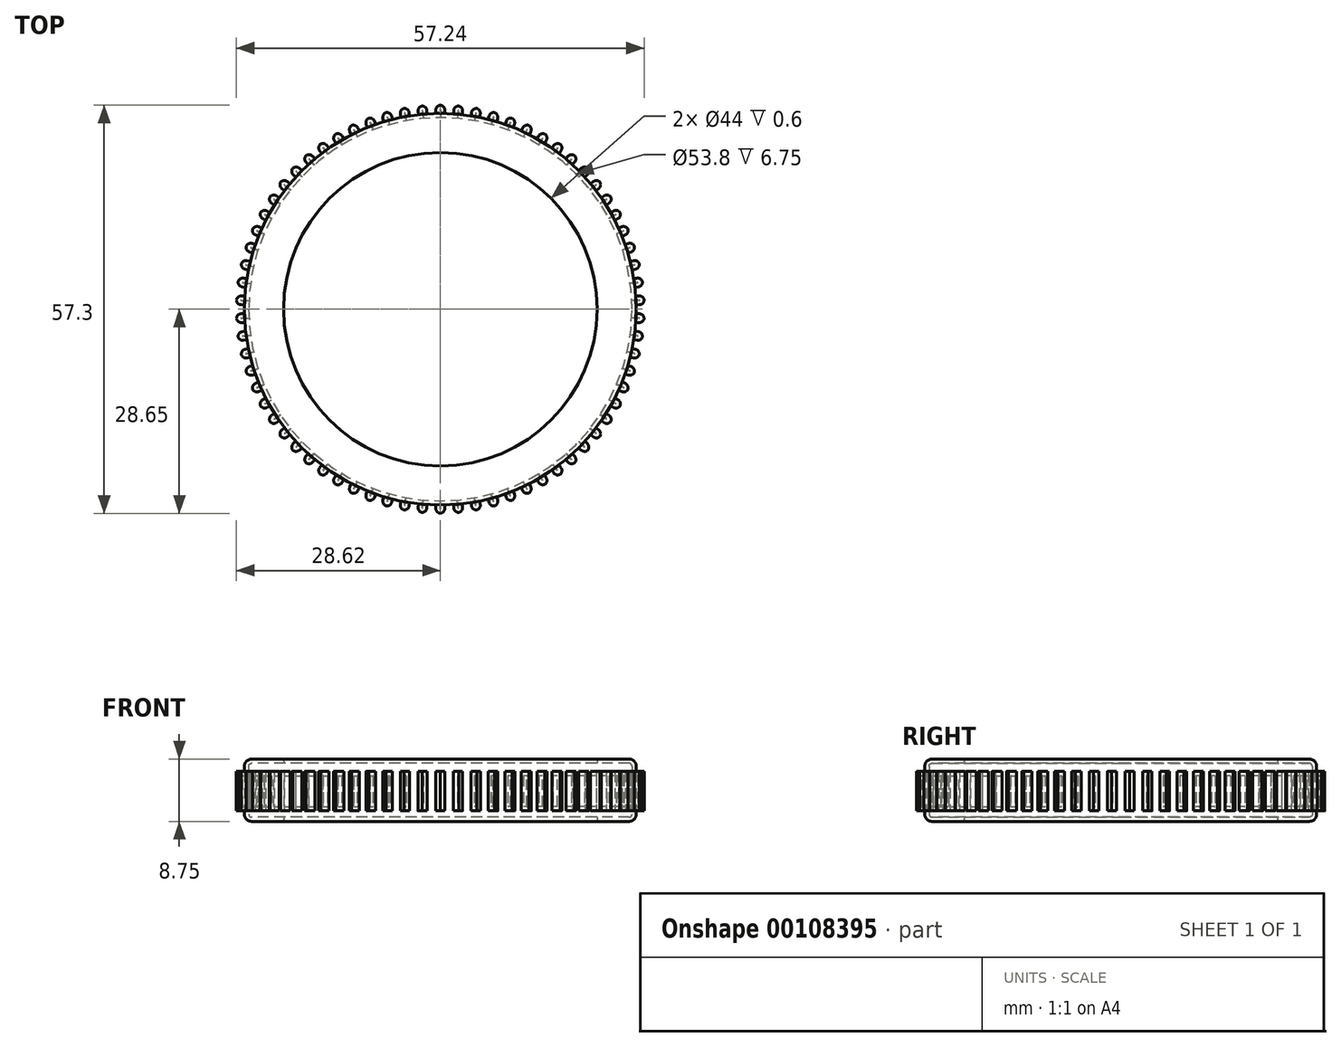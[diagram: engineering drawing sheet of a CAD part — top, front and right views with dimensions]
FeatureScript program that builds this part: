
annotation { "Feature Type Name" : "Feature", "Feature Type Description" : "" }
export const myFeature = defineFeature(function(context is Context, id is Id, definition is map)
    precondition{}
    {
        {
            var Q0;
            Q0=qCreatedBy(makeId("Top.planeOp"),FACE);
            var sketch = newSketch(context, id + "F0", { "sketchPlane" : qUnion([Q0])});
            skCircle(sketch, "E0", {"center": v(0, 0) * mm, "radius": 27.5 * mm});
            skCircle(sketch, "E1", {"center": v(0, 0) * mm, "radius": 22 * mm});
            skLineSegment(sketch, "E2", {"start": v(0, 0) * mm, "end": v(0, 27.5) * mm});
            skLineSegment(sketch, "E3", {"start": v(0, 28.65) * mm, "end": v(0.62, 28.65) * mm});
            skLineSegment(sketch, "E4", {"start": v(0, 28.65) * mm, "end": v(-0.62, 28.65) * mm});
            skLineSegment(sketch, "E5", {"start": v(-0.62, 28.65) * mm, "end": v(-0.62, 27.5) * mm});
            skLineSegment(sketch, "E6", {"start": v(0.62, 28.65) * mm, "end": v(0.62, 27.5) * mm});
            skLineSegment(sketch, "E7.1.0", {"start": v(-3.2, 28.48) * mm, "end": v(-3.09, 27.33) * mm});
            skLineSegment(sketch, "E7.1.1", {"start": v(-2.57, 28.53) * mm, "end": v(-3.2, 28.48) * mm});
            skLineSegment(sketch, "E7.1.2", {"start": v(-2.57, 28.53) * mm, "end": v(-1.95, 28.6) * mm});
            skLineSegment(sketch, "E7.1.3", {"start": v(-1.95, 28.6) * mm, "end": v(-1.84, 27.44) * mm});
            skLineSegment(sketch, "E7.2.0", {"start": v(-5.73, 28.08) * mm, "end": v(-5.52, 26.94) * mm});
            skLineSegment(sketch, "E7.2.1", {"start": v(-5.12, 28.19) * mm, "end": v(-5.73, 28.08) * mm});
            skLineSegment(sketch, "E7.2.2", {"start": v(-5.12, 28.19) * mm, "end": v(-4.5, 28.3) * mm});
            skLineSegment(sketch, "E7.2.3", {"start": v(-4.5, 28.3) * mm, "end": v(-4.3, 27.16) * mm});
            skLineSegment(sketch, "E7.3.0", {"start": v(-8.22, 27.45) * mm, "end": v(-7.92, 26.34) * mm});
            skLineSegment(sketch, "E7.3.1", {"start": v(-7.62, 27.62) * mm, "end": v(-8.22, 27.45) * mm});
            skLineSegment(sketch, "E7.3.2", {"start": v(-7.62, 27.62) * mm, "end": v(-7.02, 27.78) * mm});
            skLineSegment(sketch, "E7.3.3", {"start": v(-7.02, 27.78) * mm, "end": v(-6.71, 26.67) * mm});
            skLineSegment(sketch, "E7.4.0", {"start": v(-10.65, 26.6) * mm, "end": v(-10.25, 25.52) * mm});
            skLineSegment(sketch, "E7.4.1", {"start": v(-10.07, 26.82) * mm, "end": v(-10.65, 26.6) * mm});
            skLineSegment(sketch, "E7.4.2", {"start": v(-10.07, 26.82) * mm, "end": v(-9.48, 27.04) * mm});
            skLineSegment(sketch, "E7.4.3", {"start": v(-9.48, 27.04) * mm, "end": v(-9.08, 25.96) * mm});
            skLineSegment(sketch, "E7.5.0", {"start": v(-13, 25.54) * mm, "end": v(-12.5, 24.5) * mm});
            skLineSegment(sketch, "E7.5.1", {"start": v(-12.43, 25.81) * mm, "end": v(-13, 25.54) * mm});
            skLineSegment(sketch, "E7.5.2", {"start": v(-12.43, 25.81) * mm, "end": v(-11.87, 26.08) * mm});
            skLineSegment(sketch, "E7.5.3", {"start": v(-11.87, 26.08) * mm, "end": v(-11.37, 25.04) * mm});
            skLineSegment(sketch, "E7.6.0", {"start": v(-15.23, 24.27) * mm, "end": v(-14.64, 23.28) * mm});
            skLineSegment(sketch, "E7.6.1", {"start": v(-14.7, 24.6) * mm, "end": v(-15.23, 24.27) * mm});
            skLineSegment(sketch, "E7.6.2", {"start": v(-14.7, 24.6) * mm, "end": v(-14.16, 24.92) * mm});
            skLineSegment(sketch, "E7.6.3", {"start": v(-14.16, 24.92) * mm, "end": v(-13.56, 23.92) * mm});
            skLineSegment(sketch, "E7.7.0", {"start": v(-17.35, 22.81) * mm, "end": v(-16.67, 21.87) * mm});
            skLineSegment(sketch, "E7.7.1", {"start": v(-16.84, 23.18) * mm, "end": v(-17.35, 22.81) * mm});
            skLineSegment(sketch, "E7.7.2", {"start": v(-16.84, 23.18) * mm, "end": v(-16.33, 23.55) * mm});
            skLineSegment(sketch, "E7.7.3", {"start": v(-16.33, 23.55) * mm, "end": v(-15.65, 22.6) * mm});
            skLineSegment(sketch, "E7.8.0", {"start": v(-19.32, 21.16) * mm, "end": v(-18.56, 20.3) * mm});
            skLineSegment(sketch, "E7.8.1", {"start": v(-18.85, 21.58) * mm, "end": v(-19.32, 21.16) * mm});
            skLineSegment(sketch, "E7.8.2", {"start": v(-18.85, 21.58) * mm, "end": v(-18.38, 21.99) * mm});
            skLineSegment(sketch, "E7.8.3", {"start": v(-18.38, 21.99) * mm, "end": v(-17.62, 21.12) * mm});
            skLineSegment(sketch, "E7.9.0", {"start": v(-21.14, 19.35) * mm, "end": v(-20.3, 18.55) * mm});
            skLineSegment(sketch, "E7.9.1", {"start": v(-20.7, 19.8) * mm, "end": v(-21.14, 19.35) * mm});
            skLineSegment(sketch, "E7.9.2", {"start": v(-20.7, 19.8) * mm, "end": v(-20.28, 20.25) * mm});
            skLineSegment(sketch, "E7.9.3", {"start": v(-20.28, 20.25) * mm, "end": v(-19.44, 19.45) * mm});
            skLineSegment(sketch, "E7.10.0", {"start": v(-22.79, 17.37) * mm, "end": v(-21.88, 16.65) * mm});
            skLineSegment(sketch, "E7.10.1", {"start": v(-22.4, 17.86) * mm, "end": v(-22.79, 17.37) * mm});
            skLineSegment(sketch, "E7.10.2", {"start": v(-22.4, 17.86) * mm, "end": v(-22, 18.35) * mm});
            skLineSegment(sketch, "E7.10.3", {"start": v(-22, 18.35) * mm, "end": v(-21.1, 17.63) * mm});
            skLineSegment(sketch, "E7.11.0", {"start": v(-24.25, 15.26) * mm, "end": v(-23.29, 14.62) * mm});
            skLineSegment(sketch, "E7.11.1", {"start": v(-23.91, 15.78) * mm, "end": v(-24.25, 15.26) * mm});
            skLineSegment(sketch, "E7.11.2", {"start": v(-23.91, 15.78) * mm, "end": v(-23.57, 16.3) * mm});
            skLineSegment(sketch, "E7.11.3", {"start": v(-23.57, 16.3) * mm, "end": v(-22.6, 15.67) * mm});
            skLineSegment(sketch, "E7.12.0", {"start": v(-25.53, 13.03) * mm, "end": v(-24.5, 12.48) * mm});
            skLineSegment(sketch, "E7.12.1", {"start": v(-25.23, 13.58) * mm, "end": v(-25.53, 13.03) * mm});
            skLineSegment(sketch, "E7.12.2", {"start": v(-25.23, 13.58) * mm, "end": v(-24.93, 14.13) * mm});
            skLineSegment(sketch, "E7.12.3", {"start": v(-24.93, 14.13) * mm, "end": v(-23.91, 13.58) * mm});
            skLineSegment(sketch, "E7.13.0", {"start": v(-26.6, 10.69) * mm, "end": v(-25.53, 10.23) * mm});
            skLineSegment(sketch, "E7.13.1", {"start": v(-26.34, 11.26) * mm, "end": v(-26.6, 10.69) * mm});
            skLineSegment(sketch, "E7.13.2", {"start": v(-26.34, 11.26) * mm, "end": v(-26.1, 11.83) * mm});
            skLineSegment(sketch, "E7.13.3", {"start": v(-26.1, 11.83) * mm, "end": v(-25.03, 11.38) * mm});
            skLineSegment(sketch, "E7.14.0", {"start": v(-27.44, 8.26) * mm, "end": v(-26.34, 7.9) * mm});
            skLineSegment(sketch, "E7.14.1", {"start": v(-27.25, 8.85) * mm, "end": v(-27.44, 8.26) * mm});
            skLineSegment(sketch, "E7.14.2", {"start": v(-27.25, 8.85) * mm, "end": v(-27.05, 9.45) * mm});
            skLineSegment(sketch, "E7.14.3", {"start": v(-27.05, 9.45) * mm, "end": v(-25.95, 9.1) * mm});
            skLineSegment(sketch, "E7.15.0", {"start": v(-28.07, 5.77) * mm, "end": v(-26.94, 5.5) * mm});
            skLineSegment(sketch, "E7.15.1", {"start": v(-27.93, 6.38) * mm, "end": v(-28.07, 5.77) * mm});
            skLineSegment(sketch, "E7.15.2", {"start": v(-27.93, 6.38) * mm, "end": v(-27.8, 6.98) * mm});
            skLineSegment(sketch, "E7.15.3", {"start": v(-27.8, 6.98) * mm, "end": v(-26.66, 6.73) * mm});
            skLineSegment(sketch, "E7.16.0", {"start": v(-28.47, 3.23) * mm, "end": v(-27.33, 3.07) * mm});
            skLineSegment(sketch, "E7.16.1", {"start": v(-28.4, 3.85) * mm, "end": v(-28.47, 3.23) * mm});
            skLineSegment(sketch, "E7.16.2", {"start": v(-28.4, 3.85) * mm, "end": v(-28.3, 4.47) * mm});
            skLineSegment(sketch, "E7.16.3", {"start": v(-28.3, 4.47) * mm, "end": v(-27.16, 4.3) * mm});
            skLineSegment(sketch, "E7.17.0", {"start": v(-28.65, 0.66) * mm, "end": v(-27.5, 0.6) * mm});
            skLineSegment(sketch, "E7.17.1", {"start": v(-28.62, 1.29) * mm, "end": v(-28.65, 0.66) * mm});
            skLineSegment(sketch, "E7.17.2", {"start": v(-28.62, 1.29) * mm, "end": v(-28.6, 1.9) * mm});
            skLineSegment(sketch, "E7.17.3", {"start": v(-28.6, 1.9) * mm, "end": v(-27.44, 1.86) * mm});
            skLineSegment(sketch, "E7.18.0", {"start": v(-28.6, -1.9) * mm, "end": v(-27.44, -1.86) * mm});
            skLineSegment(sketch, "E7.18.1", {"start": v(-28.62, -1.29) * mm, "end": v(-28.6, -1.9) * mm});
            skLineSegment(sketch, "E7.18.2", {"start": v(-28.62, -1.29) * mm, "end": v(-28.65, -0.66) * mm});
            skLineSegment(sketch, "E7.18.3", {"start": v(-28.65, -0.66) * mm, "end": v(-27.5, -0.6) * mm});
            skLineSegment(sketch, "E7.19.0", {"start": v(-28.3, -4.47) * mm, "end": v(-27.16, -4.3) * mm});
            skLineSegment(sketch, "E7.19.1", {"start": v(-28.4, -3.85) * mm, "end": v(-28.3, -4.47) * mm});
            skLineSegment(sketch, "E7.19.2", {"start": v(-28.4, -3.85) * mm, "end": v(-28.47, -3.23) * mm});
            skLineSegment(sketch, "E7.19.3", {"start": v(-28.47, -3.23) * mm, "end": v(-27.33, -3.07) * mm});
            skLineSegment(sketch, "E7.20.0", {"start": v(-27.8, -6.98) * mm, "end": v(-26.66, -6.73) * mm});
            skLineSegment(sketch, "E7.20.1", {"start": v(-27.93, -6.38) * mm, "end": v(-27.8, -6.98) * mm});
            skLineSegment(sketch, "E7.20.2", {"start": v(-27.93, -6.38) * mm, "end": v(-28.07, -5.77) * mm});
            skLineSegment(sketch, "E7.20.3", {"start": v(-28.07, -5.77) * mm, "end": v(-26.94, -5.5) * mm});
            skLineSegment(sketch, "E7.21.0", {"start": v(-27.05, -9.45) * mm, "end": v(-25.95, -9.1) * mm});
            skLineSegment(sketch, "E7.21.1", {"start": v(-27.25, -8.85) * mm, "end": v(-27.05, -9.45) * mm});
            skLineSegment(sketch, "E7.21.2", {"start": v(-27.25, -8.85) * mm, "end": v(-27.44, -8.26) * mm});
            skLineSegment(sketch, "E7.21.3", {"start": v(-27.44, -8.26) * mm, "end": v(-26.34, -7.9) * mm});
            skLineSegment(sketch, "E7.22.0", {"start": v(-26.1, -11.83) * mm, "end": v(-25.03, -11.38) * mm});
            skLineSegment(sketch, "E7.22.1", {"start": v(-26.34, -11.26) * mm, "end": v(-26.1, -11.83) * mm});
            skLineSegment(sketch, "E7.22.2", {"start": v(-26.34, -11.26) * mm, "end": v(-26.6, -10.69) * mm});
            skLineSegment(sketch, "E7.22.3", {"start": v(-26.6, -10.69) * mm, "end": v(-25.53, -10.23) * mm});
            skLineSegment(sketch, "E7.23.0", {"start": v(-24.93, -14.13) * mm, "end": v(-23.91, -13.58) * mm});
            skLineSegment(sketch, "E7.23.1", {"start": v(-25.23, -13.58) * mm, "end": v(-24.93, -14.13) * mm});
            skLineSegment(sketch, "E7.23.2", {"start": v(-25.23, -13.58) * mm, "end": v(-25.53, -13.03) * mm});
            skLineSegment(sketch, "E7.23.3", {"start": v(-25.53, -13.03) * mm, "end": v(-24.5, -12.48) * mm});
            skLineSegment(sketch, "E7.24.0", {"start": v(-23.57, -16.3) * mm, "end": v(-22.6, -15.67) * mm});
            skLineSegment(sketch, "E7.24.1", {"start": v(-23.91, -15.78) * mm, "end": v(-23.57, -16.3) * mm});
            skLineSegment(sketch, "E7.24.2", {"start": v(-23.91, -15.78) * mm, "end": v(-24.25, -15.26) * mm});
            skLineSegment(sketch, "E7.24.3", {"start": v(-24.25, -15.26) * mm, "end": v(-23.29, -14.62) * mm});
            skLineSegment(sketch, "E7.25.0", {"start": v(-22, -18.35) * mm, "end": v(-21.1, -17.63) * mm});
            skLineSegment(sketch, "E7.25.1", {"start": v(-22.4, -17.86) * mm, "end": v(-22, -18.35) * mm});
            skLineSegment(sketch, "E7.25.2", {"start": v(-22.4, -17.86) * mm, "end": v(-22.79, -17.37) * mm});
            skLineSegment(sketch, "E7.25.3", {"start": v(-22.79, -17.37) * mm, "end": v(-21.88, -16.65) * mm});
            skLineSegment(sketch, "E7.26.0", {"start": v(-20.28, -20.25) * mm, "end": v(-19.44, -19.45) * mm});
            skLineSegment(sketch, "E7.26.1", {"start": v(-20.7, -19.8) * mm, "end": v(-20.28, -20.25) * mm});
            skLineSegment(sketch, "E7.26.2", {"start": v(-20.7, -19.8) * mm, "end": v(-21.14, -19.35) * mm});
            skLineSegment(sketch, "E7.26.3", {"start": v(-21.14, -19.35) * mm, "end": v(-20.3, -18.55) * mm});
            skLineSegment(sketch, "E7.27.0", {"start": v(-18.38, -21.99) * mm, "end": v(-17.62, -21.12) * mm});
            skLineSegment(sketch, "E7.27.1", {"start": v(-18.85, -21.58) * mm, "end": v(-18.38, -21.99) * mm});
            skLineSegment(sketch, "E7.27.2", {"start": v(-18.85, -21.58) * mm, "end": v(-19.32, -21.16) * mm});
            skLineSegment(sketch, "E7.27.3", {"start": v(-19.32, -21.16) * mm, "end": v(-18.56, -20.3) * mm});
            skLineSegment(sketch, "E7.28.0", {"start": v(-16.33, -23.55) * mm, "end": v(-15.65, -22.6) * mm});
            skLineSegment(sketch, "E7.28.1", {"start": v(-16.84, -23.18) * mm, "end": v(-16.33, -23.55) * mm});
            skLineSegment(sketch, "E7.28.2", {"start": v(-16.84, -23.18) * mm, "end": v(-17.35, -22.81) * mm});
            skLineSegment(sketch, "E7.28.3", {"start": v(-17.35, -22.81) * mm, "end": v(-16.67, -21.87) * mm});
            skLineSegment(sketch, "E7.29.0", {"start": v(-14.16, -24.92) * mm, "end": v(-13.56, -23.92) * mm});
            skLineSegment(sketch, "E7.29.1", {"start": v(-14.7, -24.6) * mm, "end": v(-14.16, -24.92) * mm});
            skLineSegment(sketch, "E7.29.2", {"start": v(-14.7, -24.6) * mm, "end": v(-15.23, -24.27) * mm});
            skLineSegment(sketch, "E7.29.3", {"start": v(-15.23, -24.27) * mm, "end": v(-14.64, -23.28) * mm});
            skLineSegment(sketch, "E7.30.0", {"start": v(-11.87, -26.08) * mm, "end": v(-11.37, -25.04) * mm});
            skLineSegment(sketch, "E7.30.1", {"start": v(-12.43, -25.81) * mm, "end": v(-11.87, -26.08) * mm});
            skLineSegment(sketch, "E7.30.2", {"start": v(-12.43, -25.81) * mm, "end": v(-13, -25.54) * mm});
            skLineSegment(sketch, "E7.30.3", {"start": v(-13, -25.54) * mm, "end": v(-12.5, -24.5) * mm});
            skLineSegment(sketch, "E7.31.0", {"start": v(-9.48, -27.04) * mm, "end": v(-9.08, -25.96) * mm});
            skLineSegment(sketch, "E7.31.1", {"start": v(-10.07, -26.82) * mm, "end": v(-9.48, -27.04) * mm});
            skLineSegment(sketch, "E7.31.2", {"start": v(-10.07, -26.82) * mm, "end": v(-10.65, -26.6) * mm});
            skLineSegment(sketch, "E7.31.3", {"start": v(-10.65, -26.6) * mm, "end": v(-10.25, -25.52) * mm});
            skLineSegment(sketch, "E7.32.0", {"start": v(-7.02, -27.78) * mm, "end": v(-6.71, -26.67) * mm});
            skLineSegment(sketch, "E7.32.1", {"start": v(-7.62, -27.62) * mm, "end": v(-7.02, -27.78) * mm});
            skLineSegment(sketch, "E7.32.2", {"start": v(-7.62, -27.62) * mm, "end": v(-8.22, -27.45) * mm});
            skLineSegment(sketch, "E7.32.3", {"start": v(-8.22, -27.45) * mm, "end": v(-7.92, -26.34) * mm});
            skLineSegment(sketch, "E7.33.0", {"start": v(-4.5, -28.3) * mm, "end": v(-4.3, -27.16) * mm});
            skLineSegment(sketch, "E7.33.1", {"start": v(-5.12, -28.19) * mm, "end": v(-4.5, -28.3) * mm});
            skLineSegment(sketch, "E7.33.2", {"start": v(-5.12, -28.19) * mm, "end": v(-5.73, -28.08) * mm});
            skLineSegment(sketch, "E7.33.3", {"start": v(-5.73, -28.08) * mm, "end": v(-5.52, -26.94) * mm});
            skLineSegment(sketch, "E7.34.0", {"start": v(-1.95, -28.6) * mm, "end": v(-1.84, -27.44) * mm});
            skLineSegment(sketch, "E7.34.1", {"start": v(-2.57, -28.53) * mm, "end": v(-1.95, -28.6) * mm});
            skLineSegment(sketch, "E7.34.2", {"start": v(-2.57, -28.53) * mm, "end": v(-3.2, -28.48) * mm});
            skLineSegment(sketch, "E7.34.3", {"start": v(-3.2, -28.48) * mm, "end": v(-3.09, -27.33) * mm});
            skLineSegment(sketch, "E7.35.0", {"start": v(0.62, -28.65) * mm, "end": v(0.62, -27.5) * mm});
            skLineSegment(sketch, "E7.35.1", {"start": v(0, -28.65) * mm, "end": v(0.62, -28.65) * mm});
            skLineSegment(sketch, "E7.35.2", {"start": v(0, -28.65) * mm, "end": v(-0.63, -28.65) * mm});
            skLineSegment(sketch, "E7.35.3", {"start": v(-0.63, -28.65) * mm, "end": v(-0.63, -27.5) * mm});
            skLineSegment(sketch, "E7.36.0", {"start": v(3.2, -28.48) * mm, "end": v(3.09, -27.33) * mm});
            skLineSegment(sketch, "E7.36.1", {"start": v(2.57, -28.53) * mm, "end": v(3.2, -28.48) * mm});
            skLineSegment(sketch, "E7.36.2", {"start": v(2.57, -28.53) * mm, "end": v(1.95, -28.6) * mm});
            skLineSegment(sketch, "E7.36.3", {"start": v(1.95, -28.6) * mm, "end": v(1.84, -27.44) * mm});
            skLineSegment(sketch, "E7.37.0", {"start": v(5.73, -28.08) * mm, "end": v(5.52, -26.94) * mm});
            skLineSegment(sketch, "E7.37.1", {"start": v(5.12, -28.19) * mm, "end": v(5.73, -28.08) * mm});
            skLineSegment(sketch, "E7.37.2", {"start": v(5.12, -28.19) * mm, "end": v(4.5, -28.3) * mm});
            skLineSegment(sketch, "E7.37.3", {"start": v(4.5, -28.3) * mm, "end": v(4.3, -27.16) * mm});
            skLineSegment(sketch, "E7.38.0", {"start": v(8.22, -27.45) * mm, "end": v(7.92, -26.34) * mm});
            skLineSegment(sketch, "E7.38.1", {"start": v(7.62, -27.62) * mm, "end": v(8.22, -27.45) * mm});
            skLineSegment(sketch, "E7.38.2", {"start": v(7.62, -27.62) * mm, "end": v(7.02, -27.78) * mm});
            skLineSegment(sketch, "E7.38.3", {"start": v(7.02, -27.78) * mm, "end": v(6.71, -26.67) * mm});
            skLineSegment(sketch, "E7.39.0", {"start": v(10.65, -26.6) * mm, "end": v(10.25, -25.52) * mm});
            skLineSegment(sketch, "E7.39.1", {"start": v(10.07, -26.82) * mm, "end": v(10.65, -26.6) * mm});
            skLineSegment(sketch, "E7.39.2", {"start": v(10.07, -26.82) * mm, "end": v(9.48, -27.04) * mm});
            skLineSegment(sketch, "E7.39.3", {"start": v(9.48, -27.04) * mm, "end": v(9.08, -25.96) * mm});
            skLineSegment(sketch, "E7.40.0", {"start": v(13, -25.54) * mm, "end": v(12.5, -24.5) * mm});
            skLineSegment(sketch, "E7.40.1", {"start": v(12.43, -25.81) * mm, "end": v(13, -25.54) * mm});
            skLineSegment(sketch, "E7.40.2", {"start": v(12.43, -25.81) * mm, "end": v(11.87, -26.08) * mm});
            skLineSegment(sketch, "E7.40.3", {"start": v(11.87, -26.08) * mm, "end": v(11.37, -25.04) * mm});
            skLineSegment(sketch, "E7.41.0", {"start": v(15.23, -24.27) * mm, "end": v(14.64, -23.28) * mm});
            skLineSegment(sketch, "E7.41.1", {"start": v(14.7, -24.6) * mm, "end": v(15.23, -24.27) * mm});
            skLineSegment(sketch, "E7.41.2", {"start": v(14.7, -24.6) * mm, "end": v(14.16, -24.92) * mm});
            skLineSegment(sketch, "E7.41.3", {"start": v(14.16, -24.92) * mm, "end": v(13.56, -23.92) * mm});
            skLineSegment(sketch, "E7.42.0", {"start": v(17.35, -22.81) * mm, "end": v(16.67, -21.87) * mm});
            skLineSegment(sketch, "E7.42.1", {"start": v(16.84, -23.18) * mm, "end": v(17.35, -22.81) * mm});
            skLineSegment(sketch, "E7.42.2", {"start": v(16.84, -23.18) * mm, "end": v(16.33, -23.55) * mm});
            skLineSegment(sketch, "E7.42.3", {"start": v(16.33, -23.55) * mm, "end": v(15.65, -22.6) * mm});
            skLineSegment(sketch, "E7.43.0", {"start": v(19.32, -21.16) * mm, "end": v(18.56, -20.3) * mm});
            skLineSegment(sketch, "E7.43.1", {"start": v(18.85, -21.58) * mm, "end": v(19.32, -21.16) * mm});
            skLineSegment(sketch, "E7.43.2", {"start": v(18.85, -21.58) * mm, "end": v(18.38, -21.99) * mm});
            skLineSegment(sketch, "E7.43.3", {"start": v(18.38, -21.99) * mm, "end": v(17.62, -21.12) * mm});
            skLineSegment(sketch, "E7.44.0", {"start": v(21.14, -19.35) * mm, "end": v(20.3, -18.55) * mm});
            skLineSegment(sketch, "E7.44.1", {"start": v(20.7, -19.8) * mm, "end": v(21.14, -19.35) * mm});
            skLineSegment(sketch, "E7.44.2", {"start": v(20.7, -19.8) * mm, "end": v(20.28, -20.25) * mm});
            skLineSegment(sketch, "E7.44.3", {"start": v(20.28, -20.25) * mm, "end": v(19.44, -19.45) * mm});
            skLineSegment(sketch, "E7.45.0", {"start": v(22.79, -17.37) * mm, "end": v(21.88, -16.65) * mm});
            skLineSegment(sketch, "E7.45.1", {"start": v(22.4, -17.86) * mm, "end": v(22.79, -17.37) * mm});
            skLineSegment(sketch, "E7.45.2", {"start": v(22.4, -17.86) * mm, "end": v(22, -18.35) * mm});
            skLineSegment(sketch, "E7.45.3", {"start": v(22, -18.35) * mm, "end": v(21.1, -17.63) * mm});
            skLineSegment(sketch, "E7.46.0", {"start": v(24.25, -15.26) * mm, "end": v(23.29, -14.62) * mm});
            skLineSegment(sketch, "E7.46.1", {"start": v(23.91, -15.78) * mm, "end": v(24.25, -15.26) * mm});
            skLineSegment(sketch, "E7.46.2", {"start": v(23.91, -15.78) * mm, "end": v(23.57, -16.3) * mm});
            skLineSegment(sketch, "E7.46.3", {"start": v(23.57, -16.3) * mm, "end": v(22.6, -15.67) * mm});
            skLineSegment(sketch, "E7.47.0", {"start": v(25.53, -13.03) * mm, "end": v(24.5, -12.48) * mm});
            skLineSegment(sketch, "E7.47.1", {"start": v(25.23, -13.58) * mm, "end": v(25.53, -13.03) * mm});
            skLineSegment(sketch, "E7.47.2", {"start": v(25.23, -13.58) * mm, "end": v(24.93, -14.13) * mm});
            skLineSegment(sketch, "E7.47.3", {"start": v(24.93, -14.13) * mm, "end": v(23.91, -13.58) * mm});
            skLineSegment(sketch, "E7.48.0", {"start": v(26.6, -10.69) * mm, "end": v(25.53, -10.23) * mm});
            skLineSegment(sketch, "E7.48.1", {"start": v(26.34, -11.26) * mm, "end": v(26.6, -10.69) * mm});
            skLineSegment(sketch, "E7.48.2", {"start": v(26.34, -11.26) * mm, "end": v(26.1, -11.83) * mm});
            skLineSegment(sketch, "E7.48.3", {"start": v(26.1, -11.83) * mm, "end": v(25.03, -11.38) * mm});
            skLineSegment(sketch, "E7.49.0", {"start": v(27.44, -8.26) * mm, "end": v(26.34, -7.9) * mm});
            skLineSegment(sketch, "E7.49.1", {"start": v(27.25, -8.85) * mm, "end": v(27.44, -8.26) * mm});
            skLineSegment(sketch, "E7.49.2", {"start": v(27.25, -8.85) * mm, "end": v(27.05, -9.45) * mm});
            skLineSegment(sketch, "E7.49.3", {"start": v(27.05, -9.45) * mm, "end": v(25.95, -9.1) * mm});
            skLineSegment(sketch, "E7.50.0", {"start": v(28.07, -5.77) * mm, "end": v(26.94, -5.5) * mm});
            skLineSegment(sketch, "E7.50.1", {"start": v(27.93, -6.38) * mm, "end": v(28.07, -5.77) * mm});
            skLineSegment(sketch, "E7.50.2", {"start": v(27.93, -6.38) * mm, "end": v(27.8, -6.98) * mm});
            skLineSegment(sketch, "E7.50.3", {"start": v(27.8, -6.98) * mm, "end": v(26.66, -6.73) * mm});
            skLineSegment(sketch, "E7.51.0", {"start": v(28.47, -3.23) * mm, "end": v(27.33, -3.07) * mm});
            skLineSegment(sketch, "E7.51.1", {"start": v(28.4, -3.85) * mm, "end": v(28.47, -3.23) * mm});
            skLineSegment(sketch, "E7.51.2", {"start": v(28.4, -3.85) * mm, "end": v(28.3, -4.47) * mm});
            skLineSegment(sketch, "E7.51.3", {"start": v(28.3, -4.47) * mm, "end": v(27.16, -4.3) * mm});
            skLineSegment(sketch, "E7.52.0", {"start": v(28.65, -0.66) * mm, "end": v(27.5, -0.6) * mm});
            skLineSegment(sketch, "E7.52.1", {"start": v(28.62, -1.29) * mm, "end": v(28.65, -0.66) * mm});
            skLineSegment(sketch, "E7.52.2", {"start": v(28.62, -1.29) * mm, "end": v(28.6, -1.9) * mm});
            skLineSegment(sketch, "E7.52.3", {"start": v(28.6, -1.9) * mm, "end": v(27.44, -1.86) * mm});
            skLineSegment(sketch, "E7.53.0", {"start": v(28.6, 1.9) * mm, "end": v(27.44, 1.86) * mm});
            skLineSegment(sketch, "E7.53.1", {"start": v(28.62, 1.29) * mm, "end": v(28.6, 1.9) * mm});
            skLineSegment(sketch, "E7.53.2", {"start": v(28.62, 1.29) * mm, "end": v(28.65, 0.66) * mm});
            skLineSegment(sketch, "E7.53.3", {"start": v(28.65, 0.66) * mm, "end": v(27.5, 0.6) * mm});
            skLineSegment(sketch, "E7.54.0", {"start": v(28.3, 4.47) * mm, "end": v(27.16, 4.3) * mm});
            skLineSegment(sketch, "E7.54.1", {"start": v(28.4, 3.85) * mm, "end": v(28.3, 4.47) * mm});
            skLineSegment(sketch, "E7.54.2", {"start": v(28.4, 3.85) * mm, "end": v(28.47, 3.23) * mm});
            skLineSegment(sketch, "E7.54.3", {"start": v(28.47, 3.23) * mm, "end": v(27.33, 3.07) * mm});
            skLineSegment(sketch, "E7.55.0", {"start": v(27.8, 6.98) * mm, "end": v(26.66, 6.73) * mm});
            skLineSegment(sketch, "E7.55.1", {"start": v(27.93, 6.38) * mm, "end": v(27.8, 6.98) * mm});
            skLineSegment(sketch, "E7.55.2", {"start": v(27.93, 6.38) * mm, "end": v(28.07, 5.77) * mm});
            skLineSegment(sketch, "E7.55.3", {"start": v(28.07, 5.77) * mm, "end": v(26.94, 5.5) * mm});
            skLineSegment(sketch, "E7.56.0", {"start": v(27.05, 9.45) * mm, "end": v(25.95, 9.1) * mm});
            skLineSegment(sketch, "E7.56.1", {"start": v(27.25, 8.85) * mm, "end": v(27.05, 9.45) * mm});
            skLineSegment(sketch, "E7.56.2", {"start": v(27.25, 8.85) * mm, "end": v(27.44, 8.26) * mm});
            skLineSegment(sketch, "E7.56.3", {"start": v(27.44, 8.26) * mm, "end": v(26.34, 7.9) * mm});
            skLineSegment(sketch, "E7.57.0", {"start": v(26.1, 11.83) * mm, "end": v(25.03, 11.38) * mm});
            skLineSegment(sketch, "E7.57.1", {"start": v(26.34, 11.26) * mm, "end": v(26.1, 11.83) * mm});
            skLineSegment(sketch, "E7.57.2", {"start": v(26.34, 11.26) * mm, "end": v(26.6, 10.69) * mm});
            skLineSegment(sketch, "E7.57.3", {"start": v(26.6, 10.69) * mm, "end": v(25.53, 10.23) * mm});
            skLineSegment(sketch, "E7.58.0", {"start": v(24.93, 14.13) * mm, "end": v(23.91, 13.58) * mm});
            skLineSegment(sketch, "E7.58.1", {"start": v(25.23, 13.58) * mm, "end": v(24.93, 14.13) * mm});
            skLineSegment(sketch, "E7.58.2", {"start": v(25.23, 13.58) * mm, "end": v(25.53, 13.03) * mm});
            skLineSegment(sketch, "E7.58.3", {"start": v(25.53, 13.03) * mm, "end": v(24.5, 12.48) * mm});
            skLineSegment(sketch, "E7.59.0", {"start": v(23.57, 16.3) * mm, "end": v(22.6, 15.67) * mm});
            skLineSegment(sketch, "E7.59.1", {"start": v(23.91, 15.78) * mm, "end": v(23.57, 16.3) * mm});
            skLineSegment(sketch, "E7.59.2", {"start": v(23.91, 15.78) * mm, "end": v(24.25, 15.26) * mm});
            skLineSegment(sketch, "E7.59.3", {"start": v(24.25, 15.26) * mm, "end": v(23.29, 14.62) * mm});
            skLineSegment(sketch, "E7.60.0", {"start": v(22, 18.35) * mm, "end": v(21.1, 17.63) * mm});
            skLineSegment(sketch, "E7.60.1", {"start": v(22.4, 17.86) * mm, "end": v(22, 18.35) * mm});
            skLineSegment(sketch, "E7.60.2", {"start": v(22.4, 17.86) * mm, "end": v(22.79, 17.37) * mm});
            skLineSegment(sketch, "E7.60.3", {"start": v(22.79, 17.37) * mm, "end": v(21.88, 16.65) * mm});
            skLineSegment(sketch, "E7.61.0", {"start": v(20.28, 20.25) * mm, "end": v(19.44, 19.45) * mm});
            skLineSegment(sketch, "E7.61.1", {"start": v(20.7, 19.8) * mm, "end": v(20.28, 20.25) * mm});
            skLineSegment(sketch, "E7.61.2", {"start": v(20.7, 19.8) * mm, "end": v(21.14, 19.35) * mm});
            skLineSegment(sketch, "E7.61.3", {"start": v(21.14, 19.35) * mm, "end": v(20.3, 18.55) * mm});
            skLineSegment(sketch, "E7.62.0", {"start": v(18.38, 21.99) * mm, "end": v(17.62, 21.12) * mm});
            skLineSegment(sketch, "E7.62.1", {"start": v(18.85, 21.58) * mm, "end": v(18.38, 21.99) * mm});
            skLineSegment(sketch, "E7.62.2", {"start": v(18.85, 21.58) * mm, "end": v(19.32, 21.16) * mm});
            skLineSegment(sketch, "E7.62.3", {"start": v(19.32, 21.16) * mm, "end": v(18.56, 20.3) * mm});
            skLineSegment(sketch, "E7.63.0", {"start": v(16.33, 23.55) * mm, "end": v(15.65, 22.6) * mm});
            skLineSegment(sketch, "E7.63.1", {"start": v(16.84, 23.18) * mm, "end": v(16.33, 23.55) * mm});
            skLineSegment(sketch, "E7.63.2", {"start": v(16.84, 23.18) * mm, "end": v(17.35, 22.81) * mm});
            skLineSegment(sketch, "E7.63.3", {"start": v(17.35, 22.81) * mm, "end": v(16.67, 21.87) * mm});
            skLineSegment(sketch, "E7.64.0", {"start": v(14.16, 24.92) * mm, "end": v(13.56, 23.92) * mm});
            skLineSegment(sketch, "E7.64.1", {"start": v(14.7, 24.6) * mm, "end": v(14.16, 24.92) * mm});
            skLineSegment(sketch, "E7.64.2", {"start": v(14.7, 24.6) * mm, "end": v(15.23, 24.27) * mm});
            skLineSegment(sketch, "E7.64.3", {"start": v(15.23, 24.27) * mm, "end": v(14.64, 23.28) * mm});
            skLineSegment(sketch, "E7.65.0", {"start": v(11.87, 26.08) * mm, "end": v(11.37, 25.04) * mm});
            skLineSegment(sketch, "E7.65.1", {"start": v(12.43, 25.81) * mm, "end": v(11.87, 26.08) * mm});
            skLineSegment(sketch, "E7.65.2", {"start": v(12.43, 25.81) * mm, "end": v(13, 25.54) * mm});
            skLineSegment(sketch, "E7.65.3", {"start": v(13, 25.54) * mm, "end": v(12.5, 24.5) * mm});
            skLineSegment(sketch, "E7.66.0", {"start": v(9.48, 27.04) * mm, "end": v(9.08, 25.96) * mm});
            skLineSegment(sketch, "E7.66.1", {"start": v(10.07, 26.82) * mm, "end": v(9.48, 27.04) * mm});
            skLineSegment(sketch, "E7.66.2", {"start": v(10.07, 26.82) * mm, "end": v(10.65, 26.6) * mm});
            skLineSegment(sketch, "E7.66.3", {"start": v(10.65, 26.6) * mm, "end": v(10.25, 25.52) * mm});
            skLineSegment(sketch, "E7.67.0", {"start": v(7.02, 27.78) * mm, "end": v(6.71, 26.67) * mm});
            skLineSegment(sketch, "E7.67.1", {"start": v(7.62, 27.62) * mm, "end": v(7.02, 27.78) * mm});
            skLineSegment(sketch, "E7.67.2", {"start": v(7.62, 27.62) * mm, "end": v(8.22, 27.45) * mm});
            skLineSegment(sketch, "E7.67.3", {"start": v(8.22, 27.45) * mm, "end": v(7.92, 26.34) * mm});
            skLineSegment(sketch, "E7.68.0", {"start": v(4.5, 28.3) * mm, "end": v(4.3, 27.16) * mm});
            skLineSegment(sketch, "E7.68.1", {"start": v(5.12, 28.19) * mm, "end": v(4.5, 28.3) * mm});
            skLineSegment(sketch, "E7.68.2", {"start": v(5.12, 28.19) * mm, "end": v(5.73, 28.08) * mm});
            skLineSegment(sketch, "E7.68.3", {"start": v(5.73, 28.08) * mm, "end": v(5.52, 26.94) * mm});
            skLineSegment(sketch, "E7.69.0", {"start": v(1.95, 28.6) * mm, "end": v(1.84, 27.44) * mm});
            skLineSegment(sketch, "E7.69.1", {"start": v(2.57, 28.53) * mm, "end": v(1.95, 28.6) * mm});
            skLineSegment(sketch, "E7.69.2", {"start": v(2.57, 28.53) * mm, "end": v(3.2, 28.48) * mm});
            skLineSegment(sketch, "E7.69.3", {"start": v(3.2, 28.48) * mm, "end": v(3.09, 27.33) * mm});
            skSolve(sketch);
        }
        {
            var Q0;
            {var subQ0=sQuery(id+"F0.wireOp",EDGE,"E7.53.0");Q0=makeQuery(id+"F0.imprint","IMPRINT",FACE,{"disambiguationData":[TD([[makeQuery(id+"F0.imprint","IMPRINT",EDGE,{"derivedFrom":subQ0}),1.0]])]});}
            var Q1;
            {var subQ0=sQuery(id+"F0.wireOp",EDGE,"E7.54.0");Q1=makeQuery(id+"F0.imprint","IMPRINT",FACE,{"disambiguationData":[TD([[makeQuery(id+"F0.imprint","IMPRINT",EDGE,{"derivedFrom":subQ0}),1.0]])]});}
            var Q2;
            {var subQ0=sQuery(id+"F0.wireOp",EDGE,"E7.55.0");Q2=makeQuery(id+"F0.imprint","IMPRINT",FACE,{"disambiguationData":[TD([[makeQuery(id+"F0.imprint","IMPRINT",EDGE,{"derivedFrom":subQ0}),1.0]])]});}
            var Q3;
            {var subQ1=sQuery(id+"F0.wireOp",EDGE,"E7.56.0");Q3=makeQuery(id+"F0.imprint","IMPRINT",FACE,{"disambiguationData":[TD([[makeQuery(id+"F0.imprint","IMPRINT",EDGE,{"derivedFrom":subQ1}),1.0]])]});}
            var Q4;
            {var subQ0=sQuery(id+"F0.wireOp",EDGE,"E7.57.0");Q4=makeQuery(id+"F0.imprint","IMPRINT",FACE,{"disambiguationData":[TD([[makeQuery(id+"F0.imprint","IMPRINT",EDGE,{"derivedFrom":subQ0}),1.0]])]});}
            var Q5;
            {var subQ0=sQuery(id+"F0.wireOp",EDGE,"E7.58.0");Q5=makeQuery(id+"F0.imprint","IMPRINT",FACE,{"disambiguationData":[TD([[makeQuery(id+"F0.imprint","IMPRINT",EDGE,{"derivedFrom":subQ0}),1.0]])]});}
            var Q6;
            {var subQ0=sQuery(id+"F0.wireOp",EDGE,"E7.59.0");Q6=makeQuery(id+"F0.imprint","IMPRINT",FACE,{"disambiguationData":[TD([[makeQuery(id+"F0.imprint","IMPRINT",EDGE,{"derivedFrom":subQ0}),1.0]])]});}
            var Q7;
            {var subQ0=sQuery(id+"F0.wireOp",EDGE,"E7.60.0");Q7=makeQuery(id+"F0.imprint","IMPRINT",FACE,{"disambiguationData":[TD([[makeQuery(id+"F0.imprint","IMPRINT",EDGE,{"derivedFrom":subQ0}),1.0]])]});}
            var Q8;
            {var subQ0=sQuery(id+"F0.wireOp",EDGE,"E7.61.0");Q8=makeQuery(id+"F0.imprint","IMPRINT",FACE,{"disambiguationData":[TD([[makeQuery(id+"F0.imprint","IMPRINT",EDGE,{"derivedFrom":subQ0}),1.0]])]});}
            var Q9;
            {var subQ0=sQuery(id+"F0.wireOp",EDGE,"E7.62.0");Q9=makeQuery(id+"F0.imprint","IMPRINT",FACE,{"disambiguationData":[TD([[makeQuery(id+"F0.imprint","IMPRINT",EDGE,{"derivedFrom":subQ0}),1.0]])]});}
            var Q10;
            {var subQ0=sQuery(id+"F0.wireOp",EDGE,"E7.63.0");Q10=makeQuery(id+"F0.imprint","IMPRINT",FACE,{"disambiguationData":[TD([[makeQuery(id+"F0.imprint","IMPRINT",EDGE,{"derivedFrom":subQ0}),1.0]])]});}
            var Q11;
            {var subQ0=sQuery(id+"F0.wireOp",EDGE,"E7.64.0");Q11=makeQuery(id+"F0.imprint","IMPRINT",FACE,{"disambiguationData":[TD([[makeQuery(id+"F0.imprint","IMPRINT",EDGE,{"derivedFrom":subQ0}),1.0]])]});}
            var Q12;
            {var subQ0=sQuery(id+"F0.wireOp",EDGE,"E7.65.0");Q12=makeQuery(id+"F0.imprint","IMPRINT",FACE,{"disambiguationData":[TD([[makeQuery(id+"F0.imprint","IMPRINT",EDGE,{"derivedFrom":subQ0}),1.0]])]});}
            var Q13;
            {var subQ0=sQuery(id+"F0.wireOp",EDGE,"E7.66.0");Q13=makeQuery(id+"F0.imprint","IMPRINT",FACE,{"disambiguationData":[TD([[makeQuery(id+"F0.imprint","IMPRINT",EDGE,{"derivedFrom":subQ0}),1.0]])]});}
            var Q14;
            {var subQ0=sQuery(id+"F0.wireOp",EDGE,"E7.67.0");Q14=makeQuery(id+"F0.imprint","IMPRINT",FACE,{"disambiguationData":[TD([[makeQuery(id+"F0.imprint","IMPRINT",EDGE,{"derivedFrom":subQ0}),1.0]])]});}
            var Q15;
            {var subQ0=sQuery(id+"F0.wireOp",EDGE,"E7.68.0");Q15=makeQuery(id+"F0.imprint","IMPRINT",FACE,{"disambiguationData":[TD([[makeQuery(id+"F0.imprint","IMPRINT",EDGE,{"derivedFrom":subQ0}),1.0]])]});}
            var Q16;
            {var subQ0=sQuery(id+"F0.wireOp",EDGE,"E7.69.0");Q16=makeQuery(id+"F0.imprint","IMPRINT",FACE,{"disambiguationData":[TD([[makeQuery(id+"F0.imprint","IMPRINT",EDGE,{"derivedFrom":subQ0}),1.0]])]});}
            var Q17;
            Q17=makeQuery(id+"F0.imprint","IMPRINT",FACE,{"disambiguationData":[TD([[makeQuery(id+"F0.imprint","IMPRINT",EDGE,{"derivedFrom":sQuery(id+"F0.wireOp",EDGE,"E3")}),-1.0]])]});
            var Q18;
            {var subQ0=sQuery(id+"F0.wireOp",EDGE,"E7.1.0");Q18=makeQuery(id+"F0.imprint","IMPRINT",FACE,{"disambiguationData":[TD([[makeQuery(id+"F0.imprint","IMPRINT",EDGE,{"derivedFrom":subQ0}),1.0]])]});}
            var Q19;
            {var subQ0=sQuery(id+"F0.wireOp",EDGE,"E7.2.0");Q19=makeQuery(id+"F0.imprint","IMPRINT",FACE,{"disambiguationData":[TD([[makeQuery(id+"F0.imprint","IMPRINT",EDGE,{"derivedFrom":subQ0}),1.0]])]});}
            var Q20;
            {var subQ0=sQuery(id+"F0.wireOp",EDGE,"E7.3.0");Q20=makeQuery(id+"F0.imprint","IMPRINT",FACE,{"disambiguationData":[TD([[makeQuery(id+"F0.imprint","IMPRINT",EDGE,{"derivedFrom":subQ0}),1.0]])]});}
            var Q21;
            {var subQ0=sQuery(id+"F0.wireOp",EDGE,"E7.4.0");Q21=makeQuery(id+"F0.imprint","IMPRINT",FACE,{"disambiguationData":[TD([[makeQuery(id+"F0.imprint","IMPRINT",EDGE,{"derivedFrom":subQ0}),1.0]])]});}
            var Q22;
            {var subQ0=sQuery(id+"F0.wireOp",EDGE,"E7.5.0");Q22=makeQuery(id+"F0.imprint","IMPRINT",FACE,{"disambiguationData":[TD([[makeQuery(id+"F0.imprint","IMPRINT",EDGE,{"derivedFrom":subQ0}),1.0]])]});}
            var Q23;
            {var subQ0=sQuery(id+"F0.wireOp",EDGE,"E7.6.0");Q23=makeQuery(id+"F0.imprint","IMPRINT",FACE,{"disambiguationData":[TD([[makeQuery(id+"F0.imprint","IMPRINT",EDGE,{"derivedFrom":subQ0}),1.0]])]});}
            var Q24;
            {var subQ0=sQuery(id+"F0.wireOp",EDGE,"E7.7.0");Q24=makeQuery(id+"F0.imprint","IMPRINT",FACE,{"disambiguationData":[TD([[makeQuery(id+"F0.imprint","IMPRINT",EDGE,{"derivedFrom":subQ0}),1.0]])]});}
            var Q25;
            {var subQ0=sQuery(id+"F0.wireOp",EDGE,"E7.8.0");Q25=makeQuery(id+"F0.imprint","IMPRINT",FACE,{"disambiguationData":[TD([[makeQuery(id+"F0.imprint","IMPRINT",EDGE,{"derivedFrom":subQ0}),1.0]])]});}
            var Q26;
            {var subQ0=sQuery(id+"F0.wireOp",EDGE,"E7.9.0");Q26=makeQuery(id+"F0.imprint","IMPRINT",FACE,{"disambiguationData":[TD([[makeQuery(id+"F0.imprint","IMPRINT",EDGE,{"derivedFrom":subQ0}),1.0]])]});}
            var Q27;
            {var subQ0=sQuery(id+"F0.wireOp",EDGE,"E7.10.0");Q27=makeQuery(id+"F0.imprint","IMPRINT",FACE,{"disambiguationData":[TD([[makeQuery(id+"F0.imprint","IMPRINT",EDGE,{"derivedFrom":subQ0}),1.0]])]});}
            var Q28;
            {var subQ0=sQuery(id+"F0.wireOp",EDGE,"E7.11.0");Q28=makeQuery(id+"F0.imprint","IMPRINT",FACE,{"disambiguationData":[TD([[makeQuery(id+"F0.imprint","IMPRINT",EDGE,{"derivedFrom":subQ0}),1.0]])]});}
            var Q29;
            {var subQ0=sQuery(id+"F0.wireOp",EDGE,"E7.12.0");Q29=makeQuery(id+"F0.imprint","IMPRINT",FACE,{"disambiguationData":[TD([[makeQuery(id+"F0.imprint","IMPRINT",EDGE,{"derivedFrom":subQ0}),1.0]])]});}
            var Q30;
            {var subQ0=sQuery(id+"F0.wireOp",EDGE,"E7.13.0");Q30=makeQuery(id+"F0.imprint","IMPRINT",FACE,{"disambiguationData":[TD([[makeQuery(id+"F0.imprint","IMPRINT",EDGE,{"derivedFrom":subQ0}),1.0]])]});}
            var Q31;
            {var subQ0=sQuery(id+"F0.wireOp",EDGE,"E7.14.0");Q31=makeQuery(id+"F0.imprint","IMPRINT",FACE,{"disambiguationData":[TD([[makeQuery(id+"F0.imprint","IMPRINT",EDGE,{"derivedFrom":subQ0}),1.0]])]});}
            var Q32;
            {var subQ0=sQuery(id+"F0.wireOp",EDGE,"E7.15.0");Q32=makeQuery(id+"F0.imprint","IMPRINT",FACE,{"disambiguationData":[TD([[makeQuery(id+"F0.imprint","IMPRINT",EDGE,{"derivedFrom":subQ0}),1.0]])]});}
            var Q33;
            {var subQ0=sQuery(id+"F0.wireOp",EDGE,"E7.16.0");Q33=makeQuery(id+"F0.imprint","IMPRINT",FACE,{"disambiguationData":[TD([[makeQuery(id+"F0.imprint","IMPRINT",EDGE,{"derivedFrom":subQ0}),1.0]])]});}
            var Q34;
            {var subQ0=sQuery(id+"F0.wireOp",EDGE,"E7.17.0");Q34=makeQuery(id+"F0.imprint","IMPRINT",FACE,{"disambiguationData":[TD([[makeQuery(id+"F0.imprint","IMPRINT",EDGE,{"derivedFrom":subQ0}),1.0]])]});}
            var Q35;
            {var subQ0=sQuery(id+"F0.wireOp",EDGE,"E7.18.0");Q35=makeQuery(id+"F0.imprint","IMPRINT",FACE,{"disambiguationData":[TD([[makeQuery(id+"F0.imprint","IMPRINT",EDGE,{"derivedFrom":subQ0}),1.0]])]});}
            var Q36;
            {var subQ0=sQuery(id+"F0.wireOp",EDGE,"E7.19.0");Q36=makeQuery(id+"F0.imprint","IMPRINT",FACE,{"disambiguationData":[TD([[makeQuery(id+"F0.imprint","IMPRINT",EDGE,{"derivedFrom":subQ0}),1.0]])]});}
            var Q37;
            {var subQ0=sQuery(id+"F0.wireOp",EDGE,"E7.20.0");Q37=makeQuery(id+"F0.imprint","IMPRINT",FACE,{"disambiguationData":[TD([[makeQuery(id+"F0.imprint","IMPRINT",EDGE,{"derivedFrom":subQ0}),1.0]])]});}
            var Q38;
            {var subQ0=sQuery(id+"F0.wireOp",EDGE,"E7.21.0");Q38=makeQuery(id+"F0.imprint","IMPRINT",FACE,{"disambiguationData":[TD([[makeQuery(id+"F0.imprint","IMPRINT",EDGE,{"derivedFrom":subQ0}),1.0]])]});}
            var Q39;
            {var subQ0=sQuery(id+"F0.wireOp",EDGE,"E7.22.0");Q39=makeQuery(id+"F0.imprint","IMPRINT",FACE,{"disambiguationData":[TD([[makeQuery(id+"F0.imprint","IMPRINT",EDGE,{"derivedFrom":subQ0}),1.0]])]});}
            var Q40;
            {var subQ0=sQuery(id+"F0.wireOp",EDGE,"E7.23.0");Q40=makeQuery(id+"F0.imprint","IMPRINT",FACE,{"disambiguationData":[TD([[makeQuery(id+"F0.imprint","IMPRINT",EDGE,{"derivedFrom":subQ0}),1.0]])]});}
            var Q41;
            {var subQ0=sQuery(id+"F0.wireOp",EDGE,"E7.24.0");Q41=makeQuery(id+"F0.imprint","IMPRINT",FACE,{"disambiguationData":[TD([[makeQuery(id+"F0.imprint","IMPRINT",EDGE,{"derivedFrom":subQ0}),1.0]])]});}
            var Q42;
            {var subQ0=sQuery(id+"F0.wireOp",EDGE,"E7.25.0");Q42=makeQuery(id+"F0.imprint","IMPRINT",FACE,{"disambiguationData":[TD([[makeQuery(id+"F0.imprint","IMPRINT",EDGE,{"derivedFrom":subQ0}),1.0]])]});}
            var Q43;
            {var subQ1=sQuery(id+"F0.wireOp",EDGE,"E7.26.0");Q43=makeQuery(id+"F0.imprint","IMPRINT",FACE,{"disambiguationData":[TD([[makeQuery(id+"F0.imprint","IMPRINT",EDGE,{"derivedFrom":subQ1}),1.0]])]});}
            var Q44;
            {var subQ0=sQuery(id+"F0.wireOp",EDGE,"E7.27.0");Q44=makeQuery(id+"F0.imprint","IMPRINT",FACE,{"disambiguationData":[TD([[makeQuery(id+"F0.imprint","IMPRINT",EDGE,{"derivedFrom":subQ0}),1.0]])]});}
            var Q45;
            {var subQ0=sQuery(id+"F0.wireOp",EDGE,"E7.28.0");Q45=makeQuery(id+"F0.imprint","IMPRINT",FACE,{"disambiguationData":[TD([[makeQuery(id+"F0.imprint","IMPRINT",EDGE,{"derivedFrom":subQ0}),1.0]])]});}
            var Q46;
            {var subQ0=sQuery(id+"F0.wireOp",EDGE,"E7.29.0");Q46=makeQuery(id+"F0.imprint","IMPRINT",FACE,{"disambiguationData":[TD([[makeQuery(id+"F0.imprint","IMPRINT",EDGE,{"derivedFrom":subQ0}),1.0]])]});}
            var Q47;
            {var subQ0=sQuery(id+"F0.wireOp",EDGE,"E7.30.0");Q47=makeQuery(id+"F0.imprint","IMPRINT",FACE,{"disambiguationData":[TD([[makeQuery(id+"F0.imprint","IMPRINT",EDGE,{"derivedFrom":subQ0}),1.0]])]});}
            var Q48;
            {var subQ0=sQuery(id+"F0.wireOp",EDGE,"E7.31.0");Q48=makeQuery(id+"F0.imprint","IMPRINT",FACE,{"disambiguationData":[TD([[makeQuery(id+"F0.imprint","IMPRINT",EDGE,{"derivedFrom":subQ0}),1.0]])]});}
            var Q49;
            {var subQ0=sQuery(id+"F0.wireOp",EDGE,"E7.32.0");Q49=makeQuery(id+"F0.imprint","IMPRINT",FACE,{"disambiguationData":[TD([[makeQuery(id+"F0.imprint","IMPRINT",EDGE,{"derivedFrom":subQ0}),1.0]])]});}
            var Q50;
            {var subQ0=sQuery(id+"F0.wireOp",EDGE,"E7.33.0");Q50=makeQuery(id+"F0.imprint","IMPRINT",FACE,{"disambiguationData":[TD([[makeQuery(id+"F0.imprint","IMPRINT",EDGE,{"derivedFrom":subQ0}),1.0]])]});}
            var Q51;
            {var subQ0=sQuery(id+"F0.wireOp",EDGE,"E7.34.0");Q51=makeQuery(id+"F0.imprint","IMPRINT",FACE,{"disambiguationData":[TD([[makeQuery(id+"F0.imprint","IMPRINT",EDGE,{"derivedFrom":subQ0}),1.0]])]});}
            var Q52;
            {var subQ0=sQuery(id+"F0.wireOp",EDGE,"E7.35.0");Q52=makeQuery(id+"F0.imprint","IMPRINT",FACE,{"disambiguationData":[TD([[makeQuery(id+"F0.imprint","IMPRINT",EDGE,{"derivedFrom":subQ0}),1.0]])]});}
            var Q53;
            {var subQ0=sQuery(id+"F0.wireOp",EDGE,"E7.36.0");Q53=makeQuery(id+"F0.imprint","IMPRINT",FACE,{"disambiguationData":[TD([[makeQuery(id+"F0.imprint","IMPRINT",EDGE,{"derivedFrom":subQ0}),1.0]])]});}
            var Q54;
            {var subQ0=sQuery(id+"F0.wireOp",EDGE,"E7.37.0");Q54=makeQuery(id+"F0.imprint","IMPRINT",FACE,{"disambiguationData":[TD([[makeQuery(id+"F0.imprint","IMPRINT",EDGE,{"derivedFrom":subQ0}),1.0]])]});}
            var Q55;
            {var subQ0=sQuery(id+"F0.wireOp",EDGE,"E7.38.0");Q55=makeQuery(id+"F0.imprint","IMPRINT",FACE,{"disambiguationData":[TD([[makeQuery(id+"F0.imprint","IMPRINT",EDGE,{"derivedFrom":subQ0}),1.0]])]});}
            var Q56;
            {var subQ0=sQuery(id+"F0.wireOp",EDGE,"E7.39.0");Q56=makeQuery(id+"F0.imprint","IMPRINT",FACE,{"disambiguationData":[TD([[makeQuery(id+"F0.imprint","IMPRINT",EDGE,{"derivedFrom":subQ0}),1.0]])]});}
            var Q57;
            {var subQ0=sQuery(id+"F0.wireOp",EDGE,"E7.40.0");Q57=makeQuery(id+"F0.imprint","IMPRINT",FACE,{"disambiguationData":[TD([[makeQuery(id+"F0.imprint","IMPRINT",EDGE,{"derivedFrom":subQ0}),1.0]])]});}
            var Q58;
            {var subQ1=sQuery(id+"F0.wireOp",EDGE,"E7.41.0");Q58=makeQuery(id+"F0.imprint","IMPRINT",FACE,{"disambiguationData":[TD([[makeQuery(id+"F0.imprint","IMPRINT",EDGE,{"derivedFrom":subQ1}),1.0]])]});}
            var Q59;
            {var subQ0=sQuery(id+"F0.wireOp",EDGE,"E7.42.0");Q59=makeQuery(id+"F0.imprint","IMPRINT",FACE,{"disambiguationData":[TD([[makeQuery(id+"F0.imprint","IMPRINT",EDGE,{"derivedFrom":subQ0}),1.0]])]});}
            var Q60;
            {var subQ0=sQuery(id+"F0.wireOp",EDGE,"E7.43.0");Q60=makeQuery(id+"F0.imprint","IMPRINT",FACE,{"disambiguationData":[TD([[makeQuery(id+"F0.imprint","IMPRINT",EDGE,{"derivedFrom":subQ0}),1.0]])]});}
            var Q61;
            {var subQ0=sQuery(id+"F0.wireOp",EDGE,"E7.44.0");Q61=makeQuery(id+"F0.imprint","IMPRINT",FACE,{"disambiguationData":[TD([[makeQuery(id+"F0.imprint","IMPRINT",EDGE,{"derivedFrom":subQ0}),1.0]])]});}
            var Q62;
            {var subQ0=sQuery(id+"F0.wireOp",EDGE,"E7.45.0");Q62=makeQuery(id+"F0.imprint","IMPRINT",FACE,{"disambiguationData":[TD([[makeQuery(id+"F0.imprint","IMPRINT",EDGE,{"derivedFrom":subQ0}),1.0]])]});}
            var Q63;
            {var subQ0=sQuery(id+"F0.wireOp",EDGE,"E7.46.0");Q63=makeQuery(id+"F0.imprint","IMPRINT",FACE,{"disambiguationData":[TD([[makeQuery(id+"F0.imprint","IMPRINT",EDGE,{"derivedFrom":subQ0}),1.0]])]});}
            var Q64;
            {var subQ0=sQuery(id+"F0.wireOp",EDGE,"E7.47.0");Q64=makeQuery(id+"F0.imprint","IMPRINT",FACE,{"disambiguationData":[TD([[makeQuery(id+"F0.imprint","IMPRINT",EDGE,{"derivedFrom":subQ0}),1.0]])]});}
            var Q65;
            {var subQ0=sQuery(id+"F0.wireOp",EDGE,"E7.48.0");Q65=makeQuery(id+"F0.imprint","IMPRINT",FACE,{"disambiguationData":[TD([[makeQuery(id+"F0.imprint","IMPRINT",EDGE,{"derivedFrom":subQ0}),1.0]])]});}
            var Q66;
            {var subQ0=sQuery(id+"F0.wireOp",EDGE,"E7.49.0");Q66=makeQuery(id+"F0.imprint","IMPRINT",FACE,{"disambiguationData":[TD([[makeQuery(id+"F0.imprint","IMPRINT",EDGE,{"derivedFrom":subQ0}),1.0]])]});}
            var Q67;
            {var subQ0=sQuery(id+"F0.wireOp",EDGE,"E7.50.0");Q67=makeQuery(id+"F0.imprint","IMPRINT",FACE,{"disambiguationData":[TD([[makeQuery(id+"F0.imprint","IMPRINT",EDGE,{"derivedFrom":subQ0}),1.0]])]});}
            var Q68;
            {var subQ0=sQuery(id+"F0.wireOp",EDGE,"E7.51.0");Q68=makeQuery(id+"F0.imprint","IMPRINT",FACE,{"disambiguationData":[TD([[makeQuery(id+"F0.imprint","IMPRINT",EDGE,{"derivedFrom":subQ0}),1.0]])]});}
            var Q69;
            {var subQ0=sQuery(id+"F0.wireOp",EDGE,"E7.52.0");Q69=makeQuery(id+"F0.imprint","IMPRINT",FACE,{"disambiguationData":[TD([[makeQuery(id+"F0.imprint","IMPRINT",EDGE,{"derivedFrom":subQ0}),1.0]])]});}
            extrude(context, id + "F1", {"entities" : qUnion([Q0, Q1, Q2, Q3, Q4, Q5, Q6, Q7, Q8, Q9, Q10, Q11, Q12, Q13, Q14, Q15, Q16, Q17, Q18, Q19, Q20, Q21, Q22, Q23, Q24, Q25, Q26, Q27, Q28, Q29, Q30, Q31, Q32, Q33, Q34, Q35, Q36, Q37, Q38, Q39, Q40, Q41, Q42, Q43, Q44, Q45, Q46, Q47, Q48, Q49, Q50, Q51, Q52, Q53, Q54, Q55, Q56, Q57, Q58, Q59, Q60, Q61, Q62, Q63, Q64, Q65, Q66, Q67, Q68, Q69]), "depth" : 5.5 * mm});
        }
        {
            var Q0;
            Q0=makeQuery(id+"F1.opExtrude","SWEPT_EDGE",EDGE,{"disambiguationData":[OSD([sQuery(id+"F0.wireOp",EDGE,"E7.63.2"),sQuery(id+"F0.wireOp",EDGE,"E7.63.3")])]});
            var Q1;
            Q1=makeQuery(id+"F1.opExtrude","SWEPT_EDGE",EDGE,{"disambiguationData":[OSD([sQuery(id+"F0.wireOp",EDGE,"E7.63.0"),sQuery(id+"F0.wireOp",EDGE,"E7.63.1")])]});
            var Q2;
            Q2=makeQuery(id+"F1.opExtrude","SWEPT_EDGE",EDGE,{"disambiguationData":[OSD([sQuery(id+"F0.wireOp",EDGE,"E7.62.0"),sQuery(id+"F0.wireOp",EDGE,"E7.62.1")])]});
            var Q3;
            Q3=makeQuery(id+"F1.opExtrude","SWEPT_EDGE",EDGE,{"disambiguationData":[OSD([sQuery(id+"F0.wireOp",EDGE,"E7.62.2"),sQuery(id+"F0.wireOp",EDGE,"E7.62.3")])]});
            var Q4;
            Q4=makeQuery(id+"F1.opExtrude","SWEPT_EDGE",EDGE,{"disambiguationData":[OSD([sQuery(id+"F0.wireOp",EDGE,"E7.61.0"),sQuery(id+"F0.wireOp",EDGE,"E7.61.1")])]});
            var Q5;
            Q5=makeQuery(id+"F1.opExtrude","SWEPT_EDGE",EDGE,{"disambiguationData":[OSD([sQuery(id+"F0.wireOp",EDGE,"E7.61.2"),sQuery(id+"F0.wireOp",EDGE,"E7.61.3")])]});
            var Q6;
            Q6=makeQuery(id+"F1.opExtrude","SWEPT_EDGE",EDGE,{"disambiguationData":[OSD([sQuery(id+"F0.wireOp",EDGE,"E7.60.0"),sQuery(id+"F0.wireOp",EDGE,"E7.60.1")])]});
            var Q7;
            Q7=makeQuery(id+"F1.opExtrude","SWEPT_EDGE",EDGE,{"disambiguationData":[OSD([sQuery(id+"F0.wireOp",EDGE,"E7.60.2"),sQuery(id+"F0.wireOp",EDGE,"E7.60.3")])]});
            var Q8;
            Q8=makeQuery(id+"F1.opExtrude","SWEPT_EDGE",EDGE,{"disambiguationData":[OSD([sQuery(id+"F0.wireOp",EDGE,"E7.59.0"),sQuery(id+"F0.wireOp",EDGE,"E7.59.1")])]});
            var Q9;
            Q9=makeQuery(id+"F1.opExtrude","SWEPT_EDGE",EDGE,{"disambiguationData":[OSD([sQuery(id+"F0.wireOp",EDGE,"E7.59.2"),sQuery(id+"F0.wireOp",EDGE,"E7.59.3")])]});
            var Q10;
            Q10=makeQuery(id+"F1.opExtrude","SWEPT_EDGE",EDGE,{"disambiguationData":[OSD([sQuery(id+"F0.wireOp",EDGE,"E7.58.0"),sQuery(id+"F0.wireOp",EDGE,"E7.58.1")])]});
            var Q11;
            Q11=makeQuery(id+"F1.opExtrude","SWEPT_EDGE",EDGE,{"disambiguationData":[OSD([sQuery(id+"F0.wireOp",EDGE,"E7.58.2"),sQuery(id+"F0.wireOp",EDGE,"E7.58.3")])]});
            var Q12;
            Q12=makeQuery(id+"F1.opExtrude","SWEPT_EDGE",EDGE,{"disambiguationData":[OSD([sQuery(id+"F0.wireOp",EDGE,"E7.57.0"),sQuery(id+"F0.wireOp",EDGE,"E7.57.1")])]});
            var Q13;
            Q13=makeQuery(id+"F1.opExtrude","SWEPT_EDGE",EDGE,{"disambiguationData":[OSD([sQuery(id+"F0.wireOp",EDGE,"E7.57.2"),sQuery(id+"F0.wireOp",EDGE,"E7.57.3")])]});
            var Q14;
            Q14=makeQuery(id+"F1.opExtrude","SWEPT_EDGE",EDGE,{"disambiguationData":[OSD([sQuery(id+"F0.wireOp",EDGE,"E7.56.0"),sQuery(id+"F0.wireOp",EDGE,"E7.56.1")])]});
            var Q15;
            Q15=makeQuery(id+"F1.opExtrude","SWEPT_EDGE",EDGE,{"disambiguationData":[OSD([sQuery(id+"F0.wireOp",EDGE,"E7.56.2"),sQuery(id+"F0.wireOp",EDGE,"E7.56.3")])]});
            var Q16;
            Q16=makeQuery(id+"F1.opExtrude","SWEPT_EDGE",EDGE,{"disambiguationData":[OSD([sQuery(id+"F0.wireOp",EDGE,"E7.55.0"),sQuery(id+"F0.wireOp",EDGE,"E7.55.1")])]});
            var Q17;
            Q17=makeQuery(id+"F1.opExtrude","SWEPT_EDGE",EDGE,{"disambiguationData":[OSD([sQuery(id+"F0.wireOp",EDGE,"E7.55.2"),sQuery(id+"F0.wireOp",EDGE,"E7.55.3")])]});
            var Q18;
            Q18=makeQuery(id+"F1.opExtrude","SWEPT_EDGE",EDGE,{"disambiguationData":[OSD([sQuery(id+"F0.wireOp",EDGE,"E7.54.0"),sQuery(id+"F0.wireOp",EDGE,"E7.54.1")])]});
            var Q19;
            Q19=makeQuery(id+"F1.opExtrude","SWEPT_EDGE",EDGE,{"disambiguationData":[OSD([sQuery(id+"F0.wireOp",EDGE,"E7.54.2"),sQuery(id+"F0.wireOp",EDGE,"E7.54.3")])]});
            var Q20;
            Q20=makeQuery(id+"F1.opExtrude","SWEPT_EDGE",EDGE,{"disambiguationData":[OSD([sQuery(id+"F0.wireOp",EDGE,"E7.53.0"),sQuery(id+"F0.wireOp",EDGE,"E7.53.1")])]});
            var Q21;
            Q21=makeQuery(id+"F1.opExtrude","SWEPT_EDGE",EDGE,{"disambiguationData":[OSD([sQuery(id+"F0.wireOp",EDGE,"E7.53.2"),sQuery(id+"F0.wireOp",EDGE,"E7.53.3")])]});
            var Q22;
            Q22=makeQuery(id+"F1.opExtrude","SWEPT_EDGE",EDGE,{"disambiguationData":[OSD([sQuery(id+"F0.wireOp",EDGE,"E7.52.0"),sQuery(id+"F0.wireOp",EDGE,"E7.52.1")])]});
            var Q23;
            Q23=makeQuery(id+"F1.opExtrude","SWEPT_EDGE",EDGE,{"disambiguationData":[OSD([sQuery(id+"F0.wireOp",EDGE,"E7.52.2"),sQuery(id+"F0.wireOp",EDGE,"E7.52.3")])]});
            var Q24;
            Q24=makeQuery(id+"F1.opExtrude","SWEPT_EDGE",EDGE,{"disambiguationData":[OSD([sQuery(id+"F0.wireOp",EDGE,"E7.51.0"),sQuery(id+"F0.wireOp",EDGE,"E7.51.1")])]});
            var Q25;
            Q25=makeQuery(id+"F1.opExtrude","SWEPT_EDGE",EDGE,{"disambiguationData":[OSD([sQuery(id+"F0.wireOp",EDGE,"E7.51.2"),sQuery(id+"F0.wireOp",EDGE,"E7.51.3")])]});
            var Q26;
            Q26=makeQuery(id+"F1.opExtrude","SWEPT_EDGE",EDGE,{"disambiguationData":[OSD([sQuery(id+"F0.wireOp",EDGE,"E7.50.0"),sQuery(id+"F0.wireOp",EDGE,"E7.50.1")])]});
            var Q27;
            Q27=makeQuery(id+"F1.opExtrude","SWEPT_EDGE",EDGE,{"disambiguationData":[OSD([sQuery(id+"F0.wireOp",EDGE,"E7.50.2"),sQuery(id+"F0.wireOp",EDGE,"E7.50.3")])]});
            var Q28;
            Q28=makeQuery(id+"F1.opExtrude","SWEPT_EDGE",EDGE,{"disambiguationData":[OSD([sQuery(id+"F0.wireOp",EDGE,"E7.64.2"),sQuery(id+"F0.wireOp",EDGE,"E7.64.3")])]});
            var Q29;
            Q29=makeQuery(id+"F1.opExtrude","SWEPT_EDGE",EDGE,{"disambiguationData":[OSD([sQuery(id+"F0.wireOp",EDGE,"E7.64.0"),sQuery(id+"F0.wireOp",EDGE,"E7.64.1")])]});
            var Q30;
            Q30=makeQuery(id+"F1.opExtrude","SWEPT_EDGE",EDGE,{"disambiguationData":[OSD([sQuery(id+"F0.wireOp",EDGE,"E7.65.2"),sQuery(id+"F0.wireOp",EDGE,"E7.65.3")])]});
            var Q31;
            Q31=makeQuery(id+"F1.opExtrude","SWEPT_EDGE",EDGE,{"disambiguationData":[OSD([sQuery(id+"F0.wireOp",EDGE,"E7.65.0"),sQuery(id+"F0.wireOp",EDGE,"E7.65.1")])]});
            var Q32;
            Q32=makeQuery(id+"F1.opExtrude","SWEPT_EDGE",EDGE,{"disambiguationData":[OSD([sQuery(id+"F0.wireOp",EDGE,"E7.66.2"),sQuery(id+"F0.wireOp",EDGE,"E7.66.3")])]});
            var Q33;
            Q33=makeQuery(id+"F1.opExtrude","SWEPT_EDGE",EDGE,{"disambiguationData":[OSD([sQuery(id+"F0.wireOp",EDGE,"E7.66.0"),sQuery(id+"F0.wireOp",EDGE,"E7.66.1")])]});
            var Q34;
            Q34=makeQuery(id+"F1.opExtrude","SWEPT_EDGE",EDGE,{"disambiguationData":[OSD([sQuery(id+"F0.wireOp",EDGE,"E7.67.2"),sQuery(id+"F0.wireOp",EDGE,"E7.67.3")])]});
            var Q35;
            Q35=makeQuery(id+"F1.opExtrude","SWEPT_EDGE",EDGE,{"disambiguationData":[OSD([sQuery(id+"F0.wireOp",EDGE,"E7.67.0"),sQuery(id+"F0.wireOp",EDGE,"E7.67.1")])]});
            var Q36;
            Q36=makeQuery(id+"F1.opExtrude","SWEPT_EDGE",EDGE,{"disambiguationData":[OSD([sQuery(id+"F0.wireOp",EDGE,"E7.68.2"),sQuery(id+"F0.wireOp",EDGE,"E7.68.3")])]});
            var Q37;
            Q37=makeQuery(id+"F1.opExtrude","SWEPT_EDGE",EDGE,{"disambiguationData":[OSD([sQuery(id+"F0.wireOp",EDGE,"E7.68.0"),sQuery(id+"F0.wireOp",EDGE,"E7.68.1")])]});
            var Q38;
            Q38=makeQuery(id+"F1.opExtrude","SWEPT_EDGE",EDGE,{"disambiguationData":[OSD([sQuery(id+"F0.wireOp",EDGE,"E7.69.2"),sQuery(id+"F0.wireOp",EDGE,"E7.69.3")])]});
            var Q39;
            Q39=makeQuery(id+"F1.opExtrude","SWEPT_EDGE",EDGE,{"disambiguationData":[OSD([sQuery(id+"F0.wireOp",EDGE,"E7.69.0"),sQuery(id+"F0.wireOp",EDGE,"E7.69.1")])]});
            var Q40;
            Q40=makeQuery(id+"F1.opExtrude","SWEPT_EDGE",EDGE,{"disambiguationData":[OSD([sQuery(id+"F0.wireOp",EDGE,"E3"),sQuery(id+"F0.wireOp",EDGE,"E6")])]});
            var Q41;
            Q41=makeQuery(id+"F1.opExtrude","SWEPT_EDGE",EDGE,{"disambiguationData":[OSD([sQuery(id+"F0.wireOp",EDGE,"E4"),sQuery(id+"F0.wireOp",EDGE,"E5")])]});
            var Q42;
            Q42=makeQuery(id+"F1.opExtrude","SWEPT_EDGE",EDGE,{"disambiguationData":[OSD([sQuery(id+"F0.wireOp",EDGE,"E7.1.2"),sQuery(id+"F0.wireOp",EDGE,"E7.1.3")])]});
            var Q43;
            Q43=makeQuery(id+"F1.opExtrude","SWEPT_EDGE",EDGE,{"disambiguationData":[OSD([sQuery(id+"F0.wireOp",EDGE,"E7.1.0"),sQuery(id+"F0.wireOp",EDGE,"E7.1.1")])]});
            var Q44;
            Q44=makeQuery(id+"F1.opExtrude","SWEPT_EDGE",EDGE,{"disambiguationData":[OSD([sQuery(id+"F0.wireOp",EDGE,"E7.2.2"),sQuery(id+"F0.wireOp",EDGE,"E7.2.3")])]});
            var Q45;
            Q45=makeQuery(id+"F1.opExtrude","SWEPT_EDGE",EDGE,{"disambiguationData":[OSD([sQuery(id+"F0.wireOp",EDGE,"E7.2.0"),sQuery(id+"F0.wireOp",EDGE,"E7.2.1")])]});
            var Q46;
            Q46=makeQuery(id+"F1.opExtrude","SWEPT_EDGE",EDGE,{"disambiguationData":[OSD([sQuery(id+"F0.wireOp",EDGE,"E7.3.2"),sQuery(id+"F0.wireOp",EDGE,"E7.3.3")])]});
            var Q47;
            Q47=makeQuery(id+"F1.opExtrude","SWEPT_EDGE",EDGE,{"disambiguationData":[OSD([sQuery(id+"F0.wireOp",EDGE,"E7.3.0"),sQuery(id+"F0.wireOp",EDGE,"E7.3.1")])]});
            var Q48;
            Q48=makeQuery(id+"F1.opExtrude","SWEPT_EDGE",EDGE,{"disambiguationData":[OSD([sQuery(id+"F0.wireOp",EDGE,"E7.4.2"),sQuery(id+"F0.wireOp",EDGE,"E7.4.3")])]});
            var Q49;
            Q49=makeQuery(id+"F1.opExtrude","SWEPT_EDGE",EDGE,{"disambiguationData":[OSD([sQuery(id+"F0.wireOp",EDGE,"E7.4.0"),sQuery(id+"F0.wireOp",EDGE,"E7.4.1")])]});
            var Q50;
            Q50=makeQuery(id+"F1.opExtrude","SWEPT_EDGE",EDGE,{"disambiguationData":[OSD([sQuery(id+"F0.wireOp",EDGE,"E7.5.2"),sQuery(id+"F0.wireOp",EDGE,"E7.5.3")])]});
            var Q51;
            Q51=makeQuery(id+"F1.opExtrude","SWEPT_EDGE",EDGE,{"disambiguationData":[OSD([sQuery(id+"F0.wireOp",EDGE,"E7.5.0"),sQuery(id+"F0.wireOp",EDGE,"E7.5.1")])]});
            var Q52;
            Q52=makeQuery(id+"F1.opExtrude","SWEPT_EDGE",EDGE,{"disambiguationData":[OSD([sQuery(id+"F0.wireOp",EDGE,"E7.6.2"),sQuery(id+"F0.wireOp",EDGE,"E7.6.3")])]});
            var Q53;
            Q53=makeQuery(id+"F1.opExtrude","SWEPT_EDGE",EDGE,{"disambiguationData":[OSD([sQuery(id+"F0.wireOp",EDGE,"E7.6.0"),sQuery(id+"F0.wireOp",EDGE,"E7.6.1")])]});
            var Q54;
            Q54=makeQuery(id+"F1.opExtrude","SWEPT_EDGE",EDGE,{"disambiguationData":[OSD([sQuery(id+"F0.wireOp",EDGE,"E7.7.2"),sQuery(id+"F0.wireOp",EDGE,"E7.7.3")])]});
            var Q55;
            Q55=makeQuery(id+"F1.opExtrude","SWEPT_EDGE",EDGE,{"disambiguationData":[OSD([sQuery(id+"F0.wireOp",EDGE,"E7.7.0"),sQuery(id+"F0.wireOp",EDGE,"E7.7.1")])]});
            var Q56;
            Q56=makeQuery(id+"F1.opExtrude","SWEPT_EDGE",EDGE,{"disambiguationData":[OSD([sQuery(id+"F0.wireOp",EDGE,"E7.8.2"),sQuery(id+"F0.wireOp",EDGE,"E7.8.3")])]});
            var Q57;
            Q57=makeQuery(id+"F1.opExtrude","SWEPT_EDGE",EDGE,{"disambiguationData":[OSD([sQuery(id+"F0.wireOp",EDGE,"E7.8.0"),sQuery(id+"F0.wireOp",EDGE,"E7.8.1")])]});
            var Q58;
            Q58=makeQuery(id+"F1.opExtrude","SWEPT_EDGE",EDGE,{"disambiguationData":[OSD([sQuery(id+"F0.wireOp",EDGE,"E7.9.2"),sQuery(id+"F0.wireOp",EDGE,"E7.9.3")])]});
            var Q59;
            Q59=makeQuery(id+"F1.opExtrude","SWEPT_EDGE",EDGE,{"disambiguationData":[OSD([sQuery(id+"F0.wireOp",EDGE,"E7.9.0"),sQuery(id+"F0.wireOp",EDGE,"E7.9.1")])]});
            var Q60;
            Q60=makeQuery(id+"F1.opExtrude","SWEPT_EDGE",EDGE,{"disambiguationData":[OSD([sQuery(id+"F0.wireOp",EDGE,"E7.10.2"),sQuery(id+"F0.wireOp",EDGE,"E7.10.3")])]});
            var Q61;
            Q61=makeQuery(id+"F1.opExtrude","SWEPT_EDGE",EDGE,{"disambiguationData":[OSD([sQuery(id+"F0.wireOp",EDGE,"E7.10.0"),sQuery(id+"F0.wireOp",EDGE,"E7.10.1")])]});
            var Q62;
            Q62=makeQuery(id+"F1.opExtrude","SWEPT_EDGE",EDGE,{"disambiguationData":[OSD([sQuery(id+"F0.wireOp",EDGE,"E7.11.2"),sQuery(id+"F0.wireOp",EDGE,"E7.11.3")])]});
            var Q63;
            Q63=makeQuery(id+"F1.opExtrude","SWEPT_EDGE",EDGE,{"disambiguationData":[OSD([sQuery(id+"F0.wireOp",EDGE,"E7.11.0"),sQuery(id+"F0.wireOp",EDGE,"E7.11.1")])]});
            var Q64;
            Q64=makeQuery(id+"F1.opExtrude","SWEPT_EDGE",EDGE,{"disambiguationData":[OSD([sQuery(id+"F0.wireOp",EDGE,"E7.12.2"),sQuery(id+"F0.wireOp",EDGE,"E7.12.3")])]});
            var Q65;
            Q65=makeQuery(id+"F1.opExtrude","SWEPT_EDGE",EDGE,{"disambiguationData":[OSD([sQuery(id+"F0.wireOp",EDGE,"E7.12.0"),sQuery(id+"F0.wireOp",EDGE,"E7.12.1")])]});
            var Q66;
            Q66=makeQuery(id+"F1.opExtrude","SWEPT_EDGE",EDGE,{"disambiguationData":[OSD([sQuery(id+"F0.wireOp",EDGE,"E7.13.2"),sQuery(id+"F0.wireOp",EDGE,"E7.13.3")])]});
            var Q67;
            Q67=makeQuery(id+"F1.opExtrude","SWEPT_EDGE",EDGE,{"disambiguationData":[OSD([sQuery(id+"F0.wireOp",EDGE,"E7.13.0"),sQuery(id+"F0.wireOp",EDGE,"E7.13.1")])]});
            var Q68;
            Q68=makeQuery(id+"F1.opExtrude","SWEPT_EDGE",EDGE,{"disambiguationData":[OSD([sQuery(id+"F0.wireOp",EDGE,"E7.14.2"),sQuery(id+"F0.wireOp",EDGE,"E7.14.3")])]});
            var Q69;
            Q69=makeQuery(id+"F1.opExtrude","SWEPT_EDGE",EDGE,{"disambiguationData":[OSD([sQuery(id+"F0.wireOp",EDGE,"E7.14.0"),sQuery(id+"F0.wireOp",EDGE,"E7.14.1")])]});
            var Q70;
            Q70=makeQuery(id+"F1.opExtrude","SWEPT_EDGE",EDGE,{"disambiguationData":[OSD([sQuery(id+"F0.wireOp",EDGE,"E7.15.2"),sQuery(id+"F0.wireOp",EDGE,"E7.15.3")])]});
            var Q71;
            Q71=makeQuery(id+"F1.opExtrude","SWEPT_EDGE",EDGE,{"disambiguationData":[OSD([sQuery(id+"F0.wireOp",EDGE,"E7.15.0"),sQuery(id+"F0.wireOp",EDGE,"E7.15.1")])]});
            var Q72;
            Q72=makeQuery(id+"F1.opExtrude","SWEPT_EDGE",EDGE,{"disambiguationData":[OSD([sQuery(id+"F0.wireOp",EDGE,"E7.16.2"),sQuery(id+"F0.wireOp",EDGE,"E7.16.3")])]});
            var Q73;
            Q73=makeQuery(id+"F1.opExtrude","SWEPT_EDGE",EDGE,{"disambiguationData":[OSD([sQuery(id+"F0.wireOp",EDGE,"E7.16.0"),sQuery(id+"F0.wireOp",EDGE,"E7.16.1")])]});
            var Q74;
            Q74=makeQuery(id+"F1.opExtrude","SWEPT_EDGE",EDGE,{"disambiguationData":[OSD([sQuery(id+"F0.wireOp",EDGE,"E7.17.2"),sQuery(id+"F0.wireOp",EDGE,"E7.17.3")])]});
            var Q75;
            Q75=makeQuery(id+"F1.opExtrude","SWEPT_EDGE",EDGE,{"disambiguationData":[OSD([sQuery(id+"F0.wireOp",EDGE,"E7.17.0"),sQuery(id+"F0.wireOp",EDGE,"E7.17.1")])]});
            var Q76;
            Q76=makeQuery(id+"F1.opExtrude","SWEPT_EDGE",EDGE,{"disambiguationData":[OSD([sQuery(id+"F0.wireOp",EDGE,"E7.18.2"),sQuery(id+"F0.wireOp",EDGE,"E7.18.3")])]});
            var Q77;
            Q77=makeQuery(id+"F1.opExtrude","SWEPT_EDGE",EDGE,{"disambiguationData":[OSD([sQuery(id+"F0.wireOp",EDGE,"E7.18.0"),sQuery(id+"F0.wireOp",EDGE,"E7.18.1")])]});
            var Q78;
            Q78=makeQuery(id+"F1.opExtrude","SWEPT_EDGE",EDGE,{"disambiguationData":[OSD([sQuery(id+"F0.wireOp",EDGE,"E7.19.2"),sQuery(id+"F0.wireOp",EDGE,"E7.19.3")])]});
            var Q79;
            Q79=makeQuery(id+"F1.opExtrude","SWEPT_EDGE",EDGE,{"disambiguationData":[OSD([sQuery(id+"F0.wireOp",EDGE,"E7.19.0"),sQuery(id+"F0.wireOp",EDGE,"E7.19.1")])]});
            var Q80;
            Q80=makeQuery(id+"F1.opExtrude","SWEPT_EDGE",EDGE,{"disambiguationData":[OSD([sQuery(id+"F0.wireOp",EDGE,"E7.20.2"),sQuery(id+"F0.wireOp",EDGE,"E7.20.3")])]});
            var Q81;
            Q81=makeQuery(id+"F1.opExtrude","SWEPT_EDGE",EDGE,{"disambiguationData":[OSD([sQuery(id+"F0.wireOp",EDGE,"E7.20.0"),sQuery(id+"F0.wireOp",EDGE,"E7.20.1")])]});
            var Q82;
            Q82=makeQuery(id+"F1.opExtrude","SWEPT_EDGE",EDGE,{"disambiguationData":[OSD([sQuery(id+"F0.wireOp",EDGE,"E7.21.2"),sQuery(id+"F0.wireOp",EDGE,"E7.21.3")])]});
            var Q83;
            Q83=makeQuery(id+"F1.opExtrude","SWEPT_EDGE",EDGE,{"disambiguationData":[OSD([sQuery(id+"F0.wireOp",EDGE,"E7.21.0"),sQuery(id+"F0.wireOp",EDGE,"E7.21.1")])]});
            var Q84;
            Q84=makeQuery(id+"F1.opExtrude","SWEPT_EDGE",EDGE,{"disambiguationData":[OSD([sQuery(id+"F0.wireOp",EDGE,"E7.22.2"),sQuery(id+"F0.wireOp",EDGE,"E7.22.3")])]});
            var Q85;
            Q85=makeQuery(id+"F1.opExtrude","SWEPT_EDGE",EDGE,{"disambiguationData":[OSD([sQuery(id+"F0.wireOp",EDGE,"E7.22.0"),sQuery(id+"F0.wireOp",EDGE,"E7.22.1")])]});
            var Q86;
            Q86=makeQuery(id+"F1.opExtrude","SWEPT_EDGE",EDGE,{"disambiguationData":[OSD([sQuery(id+"F0.wireOp",EDGE,"E7.23.2"),sQuery(id+"F0.wireOp",EDGE,"E7.23.3")])]});
            var Q87;
            Q87=makeQuery(id+"F1.opExtrude","SWEPT_EDGE",EDGE,{"disambiguationData":[OSD([sQuery(id+"F0.wireOp",EDGE,"E7.23.0"),sQuery(id+"F0.wireOp",EDGE,"E7.23.1")])]});
            var Q88;
            Q88=makeQuery(id+"F1.opExtrude","SWEPT_EDGE",EDGE,{"disambiguationData":[OSD([sQuery(id+"F0.wireOp",EDGE,"E7.24.2"),sQuery(id+"F0.wireOp",EDGE,"E7.24.3")])]});
            var Q89;
            Q89=makeQuery(id+"F1.opExtrude","SWEPT_EDGE",EDGE,{"disambiguationData":[OSD([sQuery(id+"F0.wireOp",EDGE,"E7.24.0"),sQuery(id+"F0.wireOp",EDGE,"E7.24.1")])]});
            var Q90;
            Q90=makeQuery(id+"F1.opExtrude","SWEPT_EDGE",EDGE,{"disambiguationData":[OSD([sQuery(id+"F0.wireOp",EDGE,"E7.25.2"),sQuery(id+"F0.wireOp",EDGE,"E7.25.3")])]});
            var Q91;
            Q91=makeQuery(id+"F1.opExtrude","SWEPT_EDGE",EDGE,{"disambiguationData":[OSD([sQuery(id+"F0.wireOp",EDGE,"E7.25.0"),sQuery(id+"F0.wireOp",EDGE,"E7.25.1")])]});
            var Q92;
            Q92=makeQuery(id+"F1.opExtrude","SWEPT_EDGE",EDGE,{"disambiguationData":[OSD([sQuery(id+"F0.wireOp",EDGE,"E7.26.2"),sQuery(id+"F0.wireOp",EDGE,"E7.26.3")])]});
            var Q93;
            Q93=makeQuery(id+"F1.opExtrude","SWEPT_EDGE",EDGE,{"disambiguationData":[OSD([sQuery(id+"F0.wireOp",EDGE,"E7.26.0"),sQuery(id+"F0.wireOp",EDGE,"E7.26.1")])]});
            var Q94;
            Q94=makeQuery(id+"F1.opExtrude","SWEPT_EDGE",EDGE,{"disambiguationData":[OSD([sQuery(id+"F0.wireOp",EDGE,"E7.27.2"),sQuery(id+"F0.wireOp",EDGE,"E7.27.3")])]});
            var Q95;
            Q95=makeQuery(id+"F1.opExtrude","SWEPT_EDGE",EDGE,{"disambiguationData":[OSD([sQuery(id+"F0.wireOp",EDGE,"E7.27.0"),sQuery(id+"F0.wireOp",EDGE,"E7.27.1")])]});
            var Q96;
            Q96=makeQuery(id+"F1.opExtrude","SWEPT_EDGE",EDGE,{"disambiguationData":[OSD([sQuery(id+"F0.wireOp",EDGE,"E7.28.2"),sQuery(id+"F0.wireOp",EDGE,"E7.28.3")])]});
            var Q97;
            Q97=makeQuery(id+"F1.opExtrude","SWEPT_EDGE",EDGE,{"disambiguationData":[OSD([sQuery(id+"F0.wireOp",EDGE,"E7.28.0"),sQuery(id+"F0.wireOp",EDGE,"E7.28.1")])]});
            var Q98;
            Q98=makeQuery(id+"F1.opExtrude","SWEPT_EDGE",EDGE,{"disambiguationData":[OSD([sQuery(id+"F0.wireOp",EDGE,"E7.29.2"),sQuery(id+"F0.wireOp",EDGE,"E7.29.3")])]});
            var Q99;
            Q99=makeQuery(id+"F1.opExtrude","SWEPT_EDGE",EDGE,{"disambiguationData":[OSD([sQuery(id+"F0.wireOp",EDGE,"E7.29.0"),sQuery(id+"F0.wireOp",EDGE,"E7.29.1")])]});
            var Q100;
            Q100=makeQuery(id+"F1.opExtrude","SWEPT_EDGE",EDGE,{"disambiguationData":[OSD([sQuery(id+"F0.wireOp",EDGE,"E7.30.2"),sQuery(id+"F0.wireOp",EDGE,"E7.30.3")])]});
            var Q101;
            Q101=makeQuery(id+"F1.opExtrude","SWEPT_EDGE",EDGE,{"disambiguationData":[OSD([sQuery(id+"F0.wireOp",EDGE,"E7.30.0"),sQuery(id+"F0.wireOp",EDGE,"E7.30.1")])]});
            var Q102;
            Q102=makeQuery(id+"F1.opExtrude","SWEPT_EDGE",EDGE,{"disambiguationData":[OSD([sQuery(id+"F0.wireOp",EDGE,"E7.31.2"),sQuery(id+"F0.wireOp",EDGE,"E7.31.3")])]});
            var Q103;
            Q103=makeQuery(id+"F1.opExtrude","SWEPT_EDGE",EDGE,{"disambiguationData":[OSD([sQuery(id+"F0.wireOp",EDGE,"E7.31.0"),sQuery(id+"F0.wireOp",EDGE,"E7.31.1")])]});
            var Q104;
            Q104=makeQuery(id+"F1.opExtrude","SWEPT_EDGE",EDGE,{"disambiguationData":[OSD([sQuery(id+"F0.wireOp",EDGE,"E7.32.2"),sQuery(id+"F0.wireOp",EDGE,"E7.32.3")])]});
            var Q105;
            Q105=makeQuery(id+"F1.opExtrude","SWEPT_EDGE",EDGE,{"disambiguationData":[OSD([sQuery(id+"F0.wireOp",EDGE,"E7.32.0"),sQuery(id+"F0.wireOp",EDGE,"E7.32.1")])]});
            var Q106;
            Q106=makeQuery(id+"F1.opExtrude","SWEPT_EDGE",EDGE,{"disambiguationData":[OSD([sQuery(id+"F0.wireOp",EDGE,"E7.33.2"),sQuery(id+"F0.wireOp",EDGE,"E7.33.3")])]});
            var Q107;
            Q107=makeQuery(id+"F1.opExtrude","SWEPT_EDGE",EDGE,{"disambiguationData":[OSD([sQuery(id+"F0.wireOp",EDGE,"E7.33.0"),sQuery(id+"F0.wireOp",EDGE,"E7.33.1")])]});
            var Q108;
            Q108=makeQuery(id+"F1.opExtrude","SWEPT_EDGE",EDGE,{"disambiguationData":[OSD([sQuery(id+"F0.wireOp",EDGE,"E7.34.2"),sQuery(id+"F0.wireOp",EDGE,"E7.34.3")])]});
            var Q109;
            Q109=makeQuery(id+"F1.opExtrude","SWEPT_EDGE",EDGE,{"disambiguationData":[OSD([sQuery(id+"F0.wireOp",EDGE,"E7.34.0"),sQuery(id+"F0.wireOp",EDGE,"E7.34.1")])]});
            var Q110;
            Q110=makeQuery(id+"F1.opExtrude","SWEPT_EDGE",EDGE,{"disambiguationData":[OSD([sQuery(id+"F0.wireOp",EDGE,"E7.35.2"),sQuery(id+"F0.wireOp",EDGE,"E7.35.3")])]});
            var Q111;
            Q111=makeQuery(id+"F1.opExtrude","SWEPT_EDGE",EDGE,{"disambiguationData":[OSD([sQuery(id+"F0.wireOp",EDGE,"E7.35.0"),sQuery(id+"F0.wireOp",EDGE,"E7.35.1")])]});
            var Q112;
            Q112=makeQuery(id+"F1.opExtrude","SWEPT_EDGE",EDGE,{"disambiguationData":[OSD([sQuery(id+"F0.wireOp",EDGE,"E7.36.2"),sQuery(id+"F0.wireOp",EDGE,"E7.36.3")])]});
            var Q113;
            Q113=makeQuery(id+"F1.opExtrude","SWEPT_EDGE",EDGE,{"disambiguationData":[OSD([sQuery(id+"F0.wireOp",EDGE,"E7.36.0"),sQuery(id+"F0.wireOp",EDGE,"E7.36.1")])]});
            var Q114;
            Q114=makeQuery(id+"F1.opExtrude","SWEPT_EDGE",EDGE,{"disambiguationData":[OSD([sQuery(id+"F0.wireOp",EDGE,"E7.37.2"),sQuery(id+"F0.wireOp",EDGE,"E7.37.3")])]});
            var Q115;
            Q115=makeQuery(id+"F1.opExtrude","SWEPT_EDGE",EDGE,{"disambiguationData":[OSD([sQuery(id+"F0.wireOp",EDGE,"E7.37.0"),sQuery(id+"F0.wireOp",EDGE,"E7.37.1")])]});
            var Q116;
            Q116=makeQuery(id+"F1.opExtrude","SWEPT_EDGE",EDGE,{"disambiguationData":[OSD([sQuery(id+"F0.wireOp",EDGE,"E7.38.2"),sQuery(id+"F0.wireOp",EDGE,"E7.38.3")])]});
            var Q117;
            Q117=makeQuery(id+"F1.opExtrude","SWEPT_EDGE",EDGE,{"disambiguationData":[OSD([sQuery(id+"F0.wireOp",EDGE,"E7.38.0"),sQuery(id+"F0.wireOp",EDGE,"E7.38.1")])]});
            var Q118;
            Q118=makeQuery(id+"F1.opExtrude","SWEPT_EDGE",EDGE,{"disambiguationData":[OSD([sQuery(id+"F0.wireOp",EDGE,"E7.39.2"),sQuery(id+"F0.wireOp",EDGE,"E7.39.3")])]});
            var Q119;
            Q119=makeQuery(id+"F1.opExtrude","SWEPT_EDGE",EDGE,{"disambiguationData":[OSD([sQuery(id+"F0.wireOp",EDGE,"E7.39.0"),sQuery(id+"F0.wireOp",EDGE,"E7.39.1")])]});
            var Q120;
            Q120=makeQuery(id+"F1.opExtrude","SWEPT_EDGE",EDGE,{"disambiguationData":[OSD([sQuery(id+"F0.wireOp",EDGE,"E7.40.2"),sQuery(id+"F0.wireOp",EDGE,"E7.40.3")])]});
            var Q121;
            Q121=makeQuery(id+"F1.opExtrude","SWEPT_EDGE",EDGE,{"disambiguationData":[OSD([sQuery(id+"F0.wireOp",EDGE,"E7.40.0"),sQuery(id+"F0.wireOp",EDGE,"E7.40.1")])]});
            var Q122;
            Q122=makeQuery(id+"F1.opExtrude","SWEPT_EDGE",EDGE,{"disambiguationData":[OSD([sQuery(id+"F0.wireOp",EDGE,"E7.41.2"),sQuery(id+"F0.wireOp",EDGE,"E7.41.3")])]});
            var Q123;
            Q123=makeQuery(id+"F1.opExtrude","SWEPT_EDGE",EDGE,{"disambiguationData":[OSD([sQuery(id+"F0.wireOp",EDGE,"E7.41.0"),sQuery(id+"F0.wireOp",EDGE,"E7.41.1")])]});
            var Q124;
            Q124=makeQuery(id+"F1.opExtrude","SWEPT_EDGE",EDGE,{"disambiguationData":[OSD([sQuery(id+"F0.wireOp",EDGE,"E7.42.2"),sQuery(id+"F0.wireOp",EDGE,"E7.42.3")])]});
            var Q125;
            Q125=makeQuery(id+"F1.opExtrude","SWEPT_EDGE",EDGE,{"disambiguationData":[OSD([sQuery(id+"F0.wireOp",EDGE,"E7.42.0"),sQuery(id+"F0.wireOp",EDGE,"E7.42.1")])]});
            var Q126;
            Q126=makeQuery(id+"F1.opExtrude","SWEPT_EDGE",EDGE,{"disambiguationData":[OSD([sQuery(id+"F0.wireOp",EDGE,"E7.43.2"),sQuery(id+"F0.wireOp",EDGE,"E7.43.3")])]});
            var Q127;
            Q127=makeQuery(id+"F1.opExtrude","SWEPT_EDGE",EDGE,{"disambiguationData":[OSD([sQuery(id+"F0.wireOp",EDGE,"E7.43.0"),sQuery(id+"F0.wireOp",EDGE,"E7.43.1")])]});
            var Q128;
            Q128=makeQuery(id+"F1.opExtrude","SWEPT_EDGE",EDGE,{"disambiguationData":[OSD([sQuery(id+"F0.wireOp",EDGE,"E7.44.2"),sQuery(id+"F0.wireOp",EDGE,"E7.44.3")])]});
            var Q129;
            Q129=makeQuery(id+"F1.opExtrude","SWEPT_EDGE",EDGE,{"disambiguationData":[OSD([sQuery(id+"F0.wireOp",EDGE,"E7.44.0"),sQuery(id+"F0.wireOp",EDGE,"E7.44.1")])]});
            var Q130;
            Q130=makeQuery(id+"F1.opExtrude","SWEPT_EDGE",EDGE,{"disambiguationData":[OSD([sQuery(id+"F0.wireOp",EDGE,"E7.45.2"),sQuery(id+"F0.wireOp",EDGE,"E7.45.3")])]});
            var Q131;
            Q131=makeQuery(id+"F1.opExtrude","SWEPT_EDGE",EDGE,{"disambiguationData":[OSD([sQuery(id+"F0.wireOp",EDGE,"E7.45.0"),sQuery(id+"F0.wireOp",EDGE,"E7.45.1")])]});
            var Q132;
            Q132=makeQuery(id+"F1.opExtrude","SWEPT_EDGE",EDGE,{"disambiguationData":[OSD([sQuery(id+"F0.wireOp",EDGE,"E7.46.2"),sQuery(id+"F0.wireOp",EDGE,"E7.46.3")])]});
            var Q133;
            Q133=makeQuery(id+"F1.opExtrude","SWEPT_EDGE",EDGE,{"disambiguationData":[OSD([sQuery(id+"F0.wireOp",EDGE,"E7.46.0"),sQuery(id+"F0.wireOp",EDGE,"E7.46.1")])]});
            var Q134;
            Q134=makeQuery(id+"F1.opExtrude","SWEPT_EDGE",EDGE,{"disambiguationData":[OSD([sQuery(id+"F0.wireOp",EDGE,"E7.47.2"),sQuery(id+"F0.wireOp",EDGE,"E7.47.3")])]});
            var Q135;
            Q135=makeQuery(id+"F1.opExtrude","SWEPT_EDGE",EDGE,{"disambiguationData":[OSD([sQuery(id+"F0.wireOp",EDGE,"E7.47.0"),sQuery(id+"F0.wireOp",EDGE,"E7.47.1")])]});
            var Q136;
            Q136=makeQuery(id+"F1.opExtrude","SWEPT_EDGE",EDGE,{"disambiguationData":[OSD([sQuery(id+"F0.wireOp",EDGE,"E7.48.2"),sQuery(id+"F0.wireOp",EDGE,"E7.48.3")])]});
            var Q137;
            Q137=makeQuery(id+"F1.opExtrude","SWEPT_EDGE",EDGE,{"disambiguationData":[OSD([sQuery(id+"F0.wireOp",EDGE,"E7.48.0"),sQuery(id+"F0.wireOp",EDGE,"E7.48.1")])]});
            var Q138;
            Q138=makeQuery(id+"F1.opExtrude","SWEPT_EDGE",EDGE,{"disambiguationData":[OSD([sQuery(id+"F0.wireOp",EDGE,"E7.49.2"),sQuery(id+"F0.wireOp",EDGE,"E7.49.3")])]});
            var Q139;
            Q139=makeQuery(id+"F1.opExtrude","SWEPT_EDGE",EDGE,{"disambiguationData":[OSD([sQuery(id+"F0.wireOp",EDGE,"E7.49.0"),sQuery(id+"F0.wireOp",EDGE,"E7.49.1")])]});
            fillet(context, id + "F2", {"entities" : qUnion([Q0, Q1, Q2, Q3, Q4, Q5, Q6, Q7, Q8, Q9, Q10, Q11, Q12, Q13, Q14, Q15, Q16, Q17, Q18, Q19, Q20, Q21, Q22, Q23, Q24, Q25, Q26, Q27, Q28, Q29, Q30, Q31, Q32, Q33, Q34, Q35, Q36, Q37, Q38, Q39, Q40, Q41, Q42, Q43, Q44, Q45, Q46, Q47, Q48, Q49, Q50, Q51, Q52, Q53, Q54, Q55, Q56, Q57, Q58, Q59, Q60, Q61, Q62, Q63, Q64, Q65, Q66, Q67, Q68, Q69, Q70, Q71, Q72, Q73, Q74, Q75, Q76, Q77, Q78, Q79, Q80, Q81, Q82, Q83, Q84, Q85, Q86, Q87, Q88, Q89, Q90, Q91, Q92, Q93, Q94, Q95, Q96, Q97, Q98, Q99, Q100, Q101, Q102, Q103, Q104, Q105, Q106, Q107, Q108, Q109, Q110, Q111, Q112, Q113, Q114, Q115, Q116, Q117, Q118, Q119, Q120, Q121, Q122, Q123, Q124, Q125, Q126, Q127, Q128, Q129, Q130, Q131, Q132, Q133, Q134, Q135, Q136, Q137, Q138, Q139]), "radius" : .7 * mm, "tangentPropagation" : true, "allowEdgeOverflow" : false});
        }
        {
            var Q0;
            Q0=makeQuery(id+"F0.imprint","IMPRINT",FACE,{"disambiguationData":[TD([[makeQuery(id+"F0.imprint","IMPRINT",EDGE,{"derivedFrom":sQuery(id+"F0.wireOp",EDGE,"E1")}),-1.0]])]});
            extrude(context, id + "F3", {"entities" : qUnion([Q0]), "operationType" : NewBodyOperationType.ADD, "depth" : 7.25 * mm});
        }
        {
            var Q0;
            Q0=makeQuery(id+"F0.imprint","IMPRINT",FACE,{"disambiguationData":[TD([[makeQuery(id+"F0.imprint","IMPRINT",EDGE,{"derivedFrom":sQuery(id+"F0.wireOp",EDGE,"E1")}),-1.0]])]});
            extrude(context, id + "F4", {"entities" : qUnion([Q0]), "operationType" : NewBodyOperationType.ADD, "oppositeDirection" : true, "depth" : 1.5 * mm});
        }
        {
            var Q0;
            Q0=makeQuery(id+"F3.opExtrude","CAP_EDGE",EDGE,{"disambiguationData":[OSD([sQuery(id+"F0.wireOp",EDGE,"E0")])],"isStart":false});
            fillet(context, id + "F5", {"entities" : qUnion([Q0]), "radius" : 1 * mm, "tangentPropagation" : true, "allowEdgeOverflow" : false});
        }
        {
            var Q0;
            Q0=makeQuery(id+"F4.opExtrude","CAP_EDGE",EDGE,{"disambiguationData":[OSD([sQuery(id+"F0.wireOp",EDGE,"E0")])],"isStart":false});
            fillet(context, id + "F6", {"entities" : qUnion([Q0]), "radius" : 1 * mm, "tangentPropagation" : true, "allowEdgeOverflow" : false});
        }
        {
            var Q0;
            {var subQ0=sQuery(id+"F0.wireOp",EDGE,"E1");Q0=makeQuery(id+"F4.boolean.opBoolean","MERGE",FACE,{"derivedFrom":[makeQuery(id+"F3.opExtrude","SWEPT_FACE",FACE,{"disambiguationData":[OSD([subQ0])]}),makeQuery(id+"F4.opExtrude","SWEPT_FACE",FACE,{"disambiguationData":[OSD([subQ0])]})]});}
            shell(context, id + "F7", {"entities" : qUnion([Q0]), "thickness" : .6 * mm});
        }
    });
